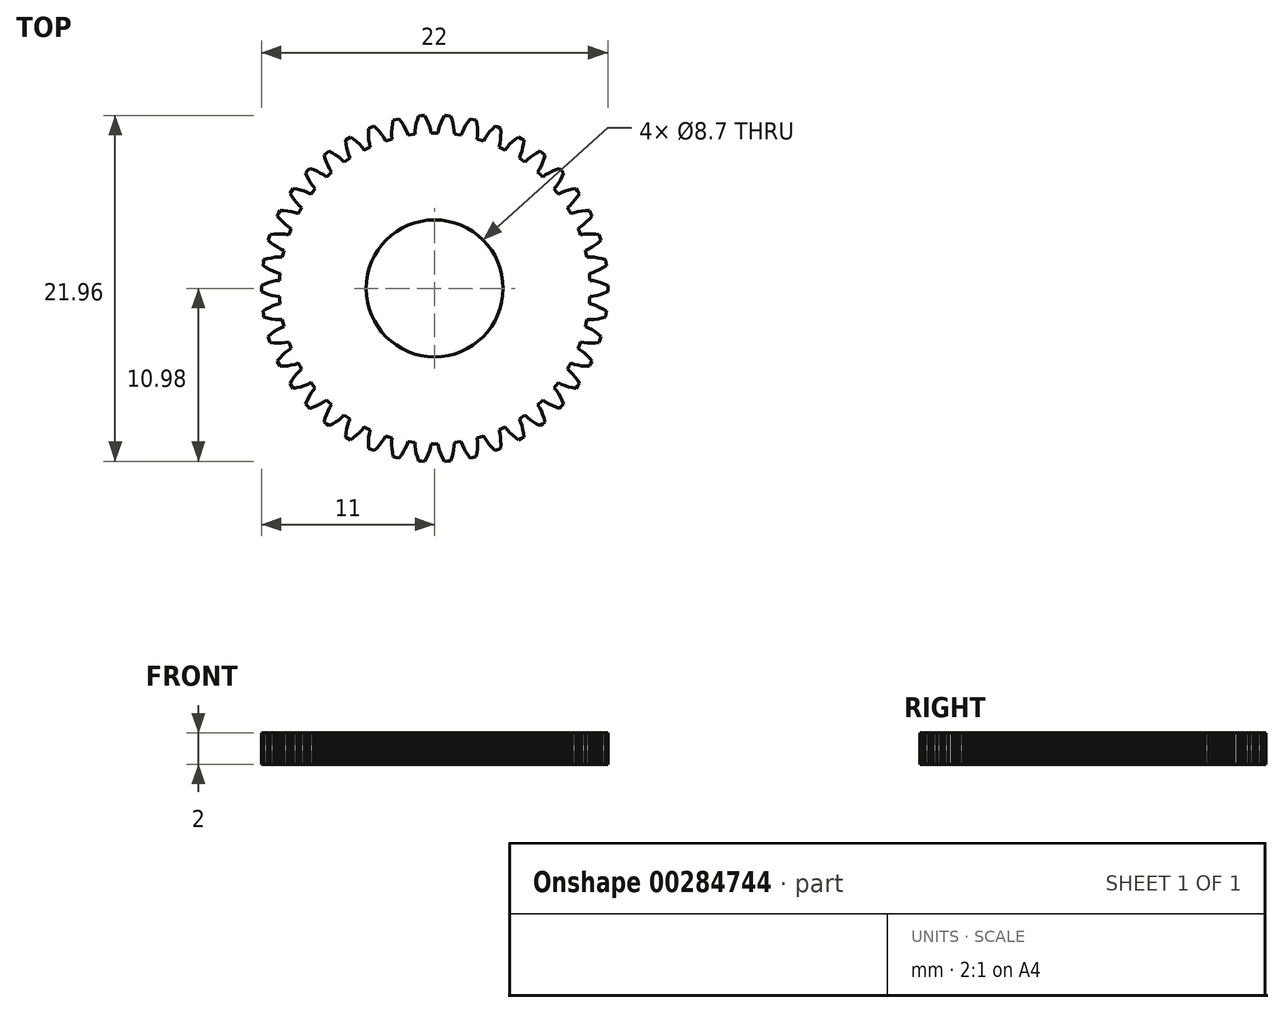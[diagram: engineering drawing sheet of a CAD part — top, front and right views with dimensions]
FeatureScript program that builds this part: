
annotation { "Feature Type Name" : "Feature", "Feature Type Description" : "" }
export const myFeature = defineFeature(function(context is Context, id is Id, definition is map)
    precondition{}
    {
        {
            var Q0;
            Q0=qCreatedBy(makeId("Top.planeOp"),FACE);
            var sketch = newSketch(context, id + "F0", { "sketchPlane" : qUnion([Q0])});
            skLineSegment(sketch, "E0", {"start": v(9.85, -0.74) * mm, "end": v(9.86, -0.52) * mm});
            skLineSegment(sketch, "E1", {"start": v(9.86, -0.52) * mm, "end": v(10.09, -0.5) * mm});
            skLineSegment(sketch, "E2", {"start": v(10.09, -0.5) * mm, "end": v(10.32, -0.44) * mm});
            skLineSegment(sketch, "E3", {"start": v(10.32, -0.44) * mm, "end": v(10.54, -0.38) * mm});
            skLineSegment(sketch, "E4", {"start": v(10.54, -0.38) * mm, "end": v(10.77, -0.3) * mm});
            skLineSegment(sketch, "E5", {"start": v(10.77, -0.3) * mm, "end": v(11, -0.2) * mm});
            skLineSegment(sketch, "E6", {"start": v(11, -0.2) * mm, "end": v(11, 0) * mm});
            skLineSegment(sketch, "E7", {"start": v(11, 0) * mm, "end": v(11, 0.2) * mm});
            skLineSegment(sketch, "E8", {"start": v(11, 0.2) * mm, "end": v(10.77, 0.3) * mm});
            skLineSegment(sketch, "E9", {"start": v(10.77, 0.3) * mm, "end": v(10.54, 0.38) * mm});
            skLineSegment(sketch, "E10", {"start": v(10.54, 0.38) * mm, "end": v(10.32, 0.44) * mm});
            skLineSegment(sketch, "E11", {"start": v(10.32, 0.44) * mm, "end": v(10.09, 0.5) * mm});
            skLineSegment(sketch, "E12", {"start": v(10.09, 0.5) * mm, "end": v(9.86, 0.52) * mm});
            skLineSegment(sketch, "E13", {"start": v(9.86, 0.52) * mm, "end": v(9.85, 0.74) * mm});
            skLineSegment(sketch, "E14", {"start": v(9.85, 0.74) * mm, "end": v(9.83, 0.96) * mm});
            skLineSegment(sketch, "E15", {"start": v(9.83, 0.96) * mm, "end": v(10.05, 1.02) * mm});
            skLineSegment(sketch, "E16", {"start": v(10.05, 1.02) * mm, "end": v(10.27, 1.1) * mm});
            skLineSegment(sketch, "E17", {"start": v(10.27, 1.1) * mm, "end": v(10.48, 1.2) * mm});
            skLineSegment(sketch, "E18", {"start": v(10.48, 1.2) * mm, "end": v(10.7, 1.32) * mm});
            skLineSegment(sketch, "E19", {"start": v(10.7, 1.32) * mm, "end": v(10.9, 1.45) * mm});
            skLineSegment(sketch, "E20", {"start": v(10.9, 1.45) * mm, "end": v(10.88, 1.64) * mm});
            skLineSegment(sketch, "E21", {"start": v(10.88, 1.64) * mm, "end": v(10.85, 1.83) * mm});
            skLineSegment(sketch, "E22", {"start": v(10.85, 1.83) * mm, "end": v(10.6, 1.9) * mm});
            skLineSegment(sketch, "E23", {"start": v(10.6, 1.9) * mm, "end": v(10.37, 1.94) * mm});
            skLineSegment(sketch, "E24", {"start": v(10.37, 1.94) * mm, "end": v(10.13, 1.98) * mm});
            skLineSegment(sketch, "E25", {"start": v(10.13, 1.98) * mm, "end": v(9.9, 2) * mm});
            skLineSegment(sketch, "E26", {"start": v(9.9, 2) * mm, "end": v(9.67, 1.98) * mm});
            skLineSegment(sketch, "E27", {"start": v(9.67, 1.98) * mm, "end": v(9.63, 2.2) * mm});
            skLineSegment(sketch, "E28", {"start": v(9.63, 2.2) * mm, "end": v(9.58, 2.41) * mm});
            skLineSegment(sketch, "E29", {"start": v(9.58, 2.41) * mm, "end": v(9.79, 2.5) * mm});
            skLineSegment(sketch, "E30", {"start": v(9.79, 2.5) * mm, "end": v(9.99, 2.62) * mm});
            skLineSegment(sketch, "E31", {"start": v(9.99, 2.62) * mm, "end": v(10.19, 2.75) * mm});
            skLineSegment(sketch, "E32", {"start": v(10.19, 2.75) * mm, "end": v(10.38, 2.9) * mm});
            skLineSegment(sketch, "E33", {"start": v(10.38, 2.9) * mm, "end": v(10.57, 3.06) * mm});
            skLineSegment(sketch, "E34", {"start": v(10.57, 3.06) * mm, "end": v(10.51, 3.24) * mm});
            skLineSegment(sketch, "E35", {"start": v(10.51, 3.24) * mm, "end": v(10.45, 3.42) * mm});
            skLineSegment(sketch, "E36", {"start": v(10.45, 3.42) * mm, "end": v(10.2, 3.45) * mm});
            skLineSegment(sketch, "E37", {"start": v(10.2, 3.45) * mm, "end": v(9.96, 3.47) * mm});
            skLineSegment(sketch, "E38", {"start": v(9.96, 3.47) * mm, "end": v(9.73, 3.47) * mm});
            skLineSegment(sketch, "E39", {"start": v(9.73, 3.47) * mm, "end": v(9.5, 3.45) * mm});
            skLineSegment(sketch, "E40", {"start": v(9.5, 3.45) * mm, "end": v(9.27, 3.4) * mm});
            skLineSegment(sketch, "E41", {"start": v(9.27, 3.4) * mm, "end": v(9.2, 3.6) * mm});
            skLineSegment(sketch, "E42", {"start": v(9.2, 3.6) * mm, "end": v(9.1, 3.81) * mm});
            skLineSegment(sketch, "E43", {"start": v(9.1, 3.81) * mm, "end": v(9.3, 3.93) * mm});
            skLineSegment(sketch, "E44", {"start": v(9.3, 3.93) * mm, "end": v(9.49, 4.08) * mm});
            skLineSegment(sketch, "E45", {"start": v(9.49, 4.08) * mm, "end": v(9.66, 4.24) * mm});
            skLineSegment(sketch, "E46", {"start": v(9.66, 4.24) * mm, "end": v(9.83, 4.41) * mm});
            skLineSegment(sketch, "E47", {"start": v(9.83, 4.41) * mm, "end": v(10, 4.6) * mm});
            skLineSegment(sketch, "E48", {"start": v(10, 4.6) * mm, "end": v(9.91, 4.77) * mm});
            skLineSegment(sketch, "E49", {"start": v(9.91, 4.77) * mm, "end": v(9.83, 4.94) * mm});
            skLineSegment(sketch, "E50", {"start": v(9.83, 4.94) * mm, "end": v(9.58, 4.94) * mm});
            skLineSegment(sketch, "E51", {"start": v(9.58, 4.94) * mm, "end": v(9.34, 4.91) * mm});
            skLineSegment(sketch, "E52", {"start": v(9.34, 4.91) * mm, "end": v(9.1, 4.88) * mm});
            skLineSegment(sketch, "E53", {"start": v(9.1, 4.88) * mm, "end": v(8.87, 4.82) * mm});
            skLineSegment(sketch, "E54", {"start": v(8.87, 4.82) * mm, "end": v(8.66, 4.74) * mm});
            skLineSegment(sketch, "E55", {"start": v(8.66, 4.74) * mm, "end": v(8.55, 4.94) * mm});
            skLineSegment(sketch, "E56", {"start": v(8.55, 4.94) * mm, "end": v(8.44, 5.13) * mm});
            skLineSegment(sketch, "E57", {"start": v(8.44, 5.13) * mm, "end": v(8.61, 5.27) * mm});
            skLineSegment(sketch, "E58", {"start": v(8.61, 5.27) * mm, "end": v(8.77, 5.44) * mm});
            skLineSegment(sketch, "E59", {"start": v(8.77, 5.44) * mm, "end": v(8.92, 5.63) * mm});
            skLineSegment(sketch, "E60", {"start": v(8.92, 5.63) * mm, "end": v(9.06, 5.83) * mm});
            skLineSegment(sketch, "E61", {"start": v(9.06, 5.83) * mm, "end": v(9.2, 6.04) * mm});
            skLineSegment(sketch, "E62", {"start": v(9.2, 6.04) * mm, "end": v(9.09, 6.2) * mm});
            skLineSegment(sketch, "E63", {"start": v(9.09, 6.2) * mm, "end": v(8.98, 6.35) * mm});
            skLineSegment(sketch, "E64", {"start": v(8.98, 6.35) * mm, "end": v(8.74, 6.3) * mm});
            skLineSegment(sketch, "E65", {"start": v(8.74, 6.3) * mm, "end": v(8.5, 6.25) * mm});
            skLineSegment(sketch, "E66", {"start": v(8.5, 6.25) * mm, "end": v(8.27, 6.18) * mm});
            skLineSegment(sketch, "E67", {"start": v(8.27, 6.18) * mm, "end": v(8.06, 6.1) * mm});
            skLineSegment(sketch, "E68", {"start": v(8.06, 6.1) * mm, "end": v(7.86, 5.98) * mm});
            skLineSegment(sketch, "E69", {"start": v(7.86, 5.98) * mm, "end": v(7.72, 6.16) * mm});
            skLineSegment(sketch, "E70", {"start": v(7.72, 6.16) * mm, "end": v(7.58, 6.33) * mm});
            skLineSegment(sketch, "E71", {"start": v(7.58, 6.33) * mm, "end": v(7.73, 6.5) * mm});
            skLineSegment(sketch, "E72", {"start": v(7.73, 6.5) * mm, "end": v(7.86, 6.7) * mm});
            skLineSegment(sketch, "E73", {"start": v(7.86, 6.7) * mm, "end": v(7.98, 6.9) * mm});
            skLineSegment(sketch, "E74", {"start": v(7.98, 6.9) * mm, "end": v(8.1, 7.11) * mm});
            skLineSegment(sketch, "E75", {"start": v(8.1, 7.11) * mm, "end": v(8.2, 7.34) * mm});
            skLineSegment(sketch, "E76", {"start": v(8.2, 7.34) * mm, "end": v(8.06, 7.48) * mm});
            skLineSegment(sketch, "E77", {"start": v(8.06, 7.48) * mm, "end": v(7.93, 7.62) * mm});
            skLineSegment(sketch, "E78", {"start": v(7.93, 7.62) * mm, "end": v(7.7, 7.54) * mm});
            skLineSegment(sketch, "E79", {"start": v(7.7, 7.54) * mm, "end": v(7.47, 7.45) * mm});
            skLineSegment(sketch, "E80", {"start": v(7.47, 7.45) * mm, "end": v(7.26, 7.34) * mm});
            skLineSegment(sketch, "E81", {"start": v(7.26, 7.34) * mm, "end": v(7.06, 7.22) * mm});
            skLineSegment(sketch, "E82", {"start": v(7.06, 7.22) * mm, "end": v(6.88, 7.09) * mm});
            skLineSegment(sketch, "E83", {"start": v(6.88, 7.09) * mm, "end": v(6.72, 7.24) * mm});
            skLineSegment(sketch, "E84", {"start": v(6.72, 7.24) * mm, "end": v(6.55, 7.39) * mm});
            skLineSegment(sketch, "E85", {"start": v(6.55, 7.39) * mm, "end": v(6.68, 7.58) * mm});
            skLineSegment(sketch, "E86", {"start": v(6.68, 7.58) * mm, "end": v(6.78, 7.79) * mm});
            skLineSegment(sketch, "E87", {"start": v(6.78, 7.79) * mm, "end": v(6.87, 8) * mm});
            skLineSegment(sketch, "E88", {"start": v(6.87, 8) * mm, "end": v(6.94, 8.24) * mm});
            skLineSegment(sketch, "E89", {"start": v(6.94, 8.24) * mm, "end": v(7, 8.48) * mm});
            skLineSegment(sketch, "E90", {"start": v(7, 8.48) * mm, "end": v(6.86, 8.6) * mm});
            skLineSegment(sketch, "E91", {"start": v(6.86, 8.6) * mm, "end": v(6.7, 8.72) * mm});
            skLineSegment(sketch, "E92", {"start": v(6.7, 8.72) * mm, "end": v(6.49, 8.6) * mm});
            skLineSegment(sketch, "E93", {"start": v(6.49, 8.6) * mm, "end": v(6.28, 8.48) * mm});
            skLineSegment(sketch, "E94", {"start": v(6.28, 8.48) * mm, "end": v(6.08, 8.34) * mm});
            skLineSegment(sketch, "E95", {"start": v(6.08, 8.34) * mm, "end": v(5.9, 8.2) * mm});
            skLineSegment(sketch, "E96", {"start": v(5.9, 8.2) * mm, "end": v(5.75, 8.03) * mm});
            skLineSegment(sketch, "E97", {"start": v(5.75, 8.03) * mm, "end": v(5.56, 8.16) * mm});
            skLineSegment(sketch, "E98", {"start": v(5.56, 8.16) * mm, "end": v(5.38, 8.28) * mm});
            skLineSegment(sketch, "E99", {"start": v(5.38, 8.28) * mm, "end": v(5.47, 8.49) * mm});
            skLineSegment(sketch, "E100", {"start": v(5.47, 8.49) * mm, "end": v(5.54, 8.71) * mm});
            skLineSegment(sketch, "E101", {"start": v(5.54, 8.71) * mm, "end": v(5.6, 8.94) * mm});
            skLineSegment(sketch, "E102", {"start": v(5.6, 8.94) * mm, "end": v(5.64, 9.18) * mm});
            skLineSegment(sketch, "E103", {"start": v(5.64, 9.18) * mm, "end": v(5.66, 9.43) * mm});
            skLineSegment(sketch, "E104", {"start": v(5.66, 9.43) * mm, "end": v(5.5, 9.53) * mm});
            skLineSegment(sketch, "E105", {"start": v(5.5, 9.53) * mm, "end": v(5.33, 9.62) * mm});
            skLineSegment(sketch, "E106", {"start": v(5.33, 9.62) * mm, "end": v(5.13, 9.47) * mm});
            skLineSegment(sketch, "E107", {"start": v(5.13, 9.47) * mm, "end": v(4.95, 9.32) * mm});
            skLineSegment(sketch, "E108", {"start": v(4.95, 9.32) * mm, "end": v(4.77, 9.16) * mm});
            skLineSegment(sketch, "E109", {"start": v(4.77, 9.16) * mm, "end": v(4.62, 8.98) * mm});
            skLineSegment(sketch, "E110", {"start": v(4.62, 8.98) * mm, "end": v(4.48, 8.8) * mm});
            skLineSegment(sketch, "E111", {"start": v(4.48, 8.8) * mm, "end": v(4.28, 8.9) * mm});
            skLineSegment(sketch, "E112", {"start": v(4.28, 8.9) * mm, "end": v(4.08, 9) * mm});
            skLineSegment(sketch, "E113", {"start": v(4.08, 9) * mm, "end": v(4.15, 9.21) * mm});
            skLineSegment(sketch, "E114", {"start": v(4.15, 9.21) * mm, "end": v(4.18, 9.44) * mm});
            skLineSegment(sketch, "E115", {"start": v(4.18, 9.44) * mm, "end": v(4.2, 9.68) * mm});
            skLineSegment(sketch, "E116", {"start": v(4.2, 9.68) * mm, "end": v(4.2, 9.92) * mm});
            skLineSegment(sketch, "E117", {"start": v(4.2, 9.92) * mm, "end": v(4.2, 10.17) * mm});
            skLineSegment(sketch, "E118", {"start": v(4.2, 10.17) * mm, "end": v(4.02, 10.24) * mm});
            skLineSegment(sketch, "E119", {"start": v(4.02, 10.24) * mm, "end": v(3.84, 10.3) * mm});
            skLineSegment(sketch, "E120", {"start": v(3.84, 10.3) * mm, "end": v(3.66, 10.13) * mm});
            skLineSegment(sketch, "E121", {"start": v(3.66, 10.13) * mm, "end": v(3.5, 9.95) * mm});
            skLineSegment(sketch, "E122", {"start": v(3.5, 9.95) * mm, "end": v(3.35, 9.76) * mm});
            skLineSegment(sketch, "E123", {"start": v(3.35, 9.76) * mm, "end": v(3.23, 9.57) * mm});
            skLineSegment(sketch, "E124", {"start": v(3.23, 9.57) * mm, "end": v(3.12, 9.37) * mm});
            skLineSegment(sketch, "E125", {"start": v(3.12, 9.37) * mm, "end": v(2.91, 9.44) * mm});
            skLineSegment(sketch, "E126", {"start": v(2.91, 9.44) * mm, "end": v(2.7, 9.5) * mm});
            skLineSegment(sketch, "E127", {"start": v(2.7, 9.5) * mm, "end": v(2.73, 9.73) * mm});
            skLineSegment(sketch, "E128", {"start": v(2.73, 9.73) * mm, "end": v(2.73, 9.96) * mm});
            skLineSegment(sketch, "E129", {"start": v(2.73, 9.96) * mm, "end": v(2.71, 10.2) * mm});
            skLineSegment(sketch, "E130", {"start": v(2.71, 10.2) * mm, "end": v(2.68, 10.44) * mm});
            skLineSegment(sketch, "E131", {"start": v(2.68, 10.44) * mm, "end": v(2.63, 10.68) * mm});
            skLineSegment(sketch, "E132", {"start": v(2.63, 10.68) * mm, "end": v(2.45, 10.72) * mm});
            skLineSegment(sketch, "E133", {"start": v(2.45, 10.72) * mm, "end": v(2.26, 10.77) * mm});
            skLineSegment(sketch, "E134", {"start": v(2.26, 10.77) * mm, "end": v(2.11, 10.57) * mm});
            skLineSegment(sketch, "E135", {"start": v(2.11, 10.57) * mm, "end": v(1.98, 10.36) * mm});
            skLineSegment(sketch, "E136", {"start": v(1.98, 10.36) * mm, "end": v(1.86, 10.16) * mm});
            skLineSegment(sketch, "E137", {"start": v(1.86, 10.16) * mm, "end": v(1.76, 9.94) * mm});
            skLineSegment(sketch, "E138", {"start": v(1.76, 9.94) * mm, "end": v(1.7, 9.73) * mm});
            skLineSegment(sketch, "E139", {"start": v(1.7, 9.73) * mm, "end": v(1.47, 9.76) * mm});
            skLineSegment(sketch, "E140", {"start": v(1.47, 9.76) * mm, "end": v(1.25, 9.8) * mm});
            skLineSegment(sketch, "E141", {"start": v(1.25, 9.8) * mm, "end": v(1.25, 10.02) * mm});
            skLineSegment(sketch, "E142", {"start": v(1.25, 10.02) * mm, "end": v(1.21, 10.25) * mm});
            skLineSegment(sketch, "E143", {"start": v(1.21, 10.25) * mm, "end": v(1.16, 10.49) * mm});
            skLineSegment(sketch, "E144", {"start": v(1.16, 10.49) * mm, "end": v(1.1, 10.72) * mm});
            skLineSegment(sketch, "E145", {"start": v(1.1, 10.72) * mm, "end": v(1.01, 10.95) * mm});
            skLineSegment(sketch, "E146", {"start": v(1.01, 10.95) * mm, "end": v(0.82, 10.97) * mm});
            skLineSegment(sketch, "E147", {"start": v(0.82, 10.97) * mm, "end": v(0.63, 10.98) * mm});
            skLineSegment(sketch, "E148", {"start": v(0.63, 10.98) * mm, "end": v(0.51, 10.76) * mm});
            skLineSegment(sketch, "E149", {"start": v(0.51, 10.76) * mm, "end": v(0.41, 10.54) * mm});
            skLineSegment(sketch, "E150", {"start": v(0.41, 10.54) * mm, "end": v(0.33, 10.32) * mm});
            skLineSegment(sketch, "E151", {"start": v(0.33, 10.32) * mm, "end": v(0.26, 10.1) * mm});
            skLineSegment(sketch, "E152", {"start": v(0.26, 10.1) * mm, "end": v(0.22, 9.87) * mm});
            skLineSegment(sketch, "E153", {"start": v(0.22, 9.87) * mm, "end": v(0, 9.88) * mm});
            skLineSegment(sketch, "E154", {"start": v(0, 9.88) * mm, "end": v(-0.22, 9.87) * mm});
            skLineSegment(sketch, "E155", {"start": v(-0.22, 9.87) * mm, "end": v(-0.26, 10.1) * mm});
            skLineSegment(sketch, "E156", {"start": v(-0.26, 10.1) * mm, "end": v(-0.33, 10.32) * mm});
            skLineSegment(sketch, "E157", {"start": v(-0.33, 10.32) * mm, "end": v(-0.41, 10.54) * mm});
            skLineSegment(sketch, "E158", {"start": v(-0.41, 10.54) * mm, "end": v(-0.51, 10.76) * mm});
            skLineSegment(sketch, "E159", {"start": v(-0.51, 10.76) * mm, "end": v(-0.63, 10.98) * mm});
            skLineSegment(sketch, "E160", {"start": v(-0.63, 10.98) * mm, "end": v(-0.82, 10.97) * mm});
            skLineSegment(sketch, "E161", {"start": v(-0.82, 10.97) * mm, "end": v(-1.01, 10.95) * mm});
            skLineSegment(sketch, "E162", {"start": v(-1.01, 10.95) * mm, "end": v(-1.1, 10.72) * mm});
            skLineSegment(sketch, "E163", {"start": v(-1.1, 10.72) * mm, "end": v(-1.16, 10.49) * mm});
            skLineSegment(sketch, "E164", {"start": v(-1.16, 10.49) * mm, "end": v(-1.21, 10.25) * mm});
            skLineSegment(sketch, "E165", {"start": v(-1.21, 10.25) * mm, "end": v(-1.25, 10.02) * mm});
            skLineSegment(sketch, "E166", {"start": v(-1.25, 10.02) * mm, "end": v(-1.25, 9.8) * mm});
            skLineSegment(sketch, "E167", {"start": v(-1.25, 9.8) * mm, "end": v(-1.47, 9.76) * mm});
            skLineSegment(sketch, "E168", {"start": v(-1.47, 9.76) * mm, "end": v(-1.7, 9.73) * mm});
            skLineSegment(sketch, "E169", {"start": v(-1.7, 9.73) * mm, "end": v(-1.76, 9.94) * mm});
            skLineSegment(sketch, "E170", {"start": v(-1.76, 9.94) * mm, "end": v(-1.86, 10.16) * mm});
            skLineSegment(sketch, "E171", {"start": v(-1.86, 10.16) * mm, "end": v(-1.98, 10.36) * mm});
            skLineSegment(sketch, "E172", {"start": v(-1.98, 10.36) * mm, "end": v(-2.11, 10.57) * mm});
            skLineSegment(sketch, "E173", {"start": v(-2.11, 10.57) * mm, "end": v(-2.26, 10.77) * mm});
            skLineSegment(sketch, "E174", {"start": v(-2.26, 10.77) * mm, "end": v(-2.45, 10.72) * mm});
            skLineSegment(sketch, "E175", {"start": v(-2.45, 10.72) * mm, "end": v(-2.63, 10.68) * mm});
            skLineSegment(sketch, "E176", {"start": v(-2.63, 10.68) * mm, "end": v(-2.68, 10.44) * mm});
            skLineSegment(sketch, "E177", {"start": v(-2.68, 10.44) * mm, "end": v(-2.71, 10.2) * mm});
            skLineSegment(sketch, "E178", {"start": v(-2.71, 10.2) * mm, "end": v(-2.73, 9.96) * mm});
            skLineSegment(sketch, "E179", {"start": v(-2.73, 9.96) * mm, "end": v(-2.73, 9.73) * mm});
            skLineSegment(sketch, "E180", {"start": v(-2.73, 9.73) * mm, "end": v(-2.7, 9.5) * mm});
            skLineSegment(sketch, "E181", {"start": v(-2.7, 9.5) * mm, "end": v(-2.91, 9.44) * mm});
            skLineSegment(sketch, "E182", {"start": v(-2.91, 9.44) * mm, "end": v(-3.12, 9.37) * mm});
            skLineSegment(sketch, "E183", {"start": v(-3.12, 9.37) * mm, "end": v(-3.23, 9.57) * mm});
            skLineSegment(sketch, "E184", {"start": v(-3.23, 9.57) * mm, "end": v(-3.35, 9.76) * mm});
            skLineSegment(sketch, "E185", {"start": v(-3.35, 9.76) * mm, "end": v(-3.5, 9.95) * mm});
            skLineSegment(sketch, "E186", {"start": v(-3.5, 9.95) * mm, "end": v(-3.66, 10.13) * mm});
            skLineSegment(sketch, "E187", {"start": v(-3.66, 10.13) * mm, "end": v(-3.84, 10.3) * mm});
            skLineSegment(sketch, "E188", {"start": v(-3.84, 10.3) * mm, "end": v(-4.02, 10.24) * mm});
            skLineSegment(sketch, "E189", {"start": v(-4.02, 10.24) * mm, "end": v(-4.2, 10.17) * mm});
            skLineSegment(sketch, "E190", {"start": v(-4.2, 10.17) * mm, "end": v(-4.2, 9.92) * mm});
            skLineSegment(sketch, "E191", {"start": v(-4.2, 9.92) * mm, "end": v(-4.2, 9.68) * mm});
            skLineSegment(sketch, "E192", {"start": v(-4.2, 9.68) * mm, "end": v(-4.18, 9.44) * mm});
            skLineSegment(sketch, "E193", {"start": v(-4.18, 9.44) * mm, "end": v(-4.15, 9.21) * mm});
            skLineSegment(sketch, "E194", {"start": v(-4.15, 9.21) * mm, "end": v(-4.08, 9) * mm});
            skLineSegment(sketch, "E195", {"start": v(-4.08, 9) * mm, "end": v(-4.28, 8.9) * mm});
            skLineSegment(sketch, "E196", {"start": v(-4.28, 8.9) * mm, "end": v(-4.48, 8.8) * mm});
            skLineSegment(sketch, "E197", {"start": v(-4.48, 8.8) * mm, "end": v(-4.62, 8.98) * mm});
            skLineSegment(sketch, "E198", {"start": v(-4.62, 8.98) * mm, "end": v(-4.77, 9.16) * mm});
            skLineSegment(sketch, "E199", {"start": v(-4.77, 9.16) * mm, "end": v(-4.95, 9.32) * mm});
            skLineSegment(sketch, "E200", {"start": v(-4.95, 9.32) * mm, "end": v(-5.13, 9.47) * mm});
            skLineSegment(sketch, "E201", {"start": v(-5.13, 9.47) * mm, "end": v(-5.33, 9.62) * mm});
            skLineSegment(sketch, "E202", {"start": v(-5.33, 9.62) * mm, "end": v(-5.5, 9.53) * mm});
            skLineSegment(sketch, "E203", {"start": v(-5.5, 9.53) * mm, "end": v(-5.66, 9.43) * mm});
            skLineSegment(sketch, "E204", {"start": v(-5.66, 9.43) * mm, "end": v(-5.64, 9.18) * mm});
            skLineSegment(sketch, "E205", {"start": v(-5.64, 9.18) * mm, "end": v(-5.6, 8.94) * mm});
            skLineSegment(sketch, "E206", {"start": v(-5.6, 8.94) * mm, "end": v(-5.54, 8.71) * mm});
            skLineSegment(sketch, "E207", {"start": v(-5.54, 8.71) * mm, "end": v(-5.47, 8.49) * mm});
            skLineSegment(sketch, "E208", {"start": v(-5.47, 8.49) * mm, "end": v(-5.38, 8.28) * mm});
            skLineSegment(sketch, "E209", {"start": v(-5.38, 8.28) * mm, "end": v(-5.56, 8.16) * mm});
            skLineSegment(sketch, "E210", {"start": v(-5.56, 8.16) * mm, "end": v(-5.75, 8.03) * mm});
            skLineSegment(sketch, "E211", {"start": v(-5.75, 8.03) * mm, "end": v(-5.9, 8.2) * mm});
            skLineSegment(sketch, "E212", {"start": v(-5.9, 8.2) * mm, "end": v(-6.08, 8.34) * mm});
            skLineSegment(sketch, "E213", {"start": v(-6.08, 8.34) * mm, "end": v(-6.28, 8.48) * mm});
            skLineSegment(sketch, "E214", {"start": v(-6.28, 8.48) * mm, "end": v(-6.49, 8.6) * mm});
            skLineSegment(sketch, "E215", {"start": v(-6.49, 8.6) * mm, "end": v(-6.7, 8.72) * mm});
            skLineSegment(sketch, "E216", {"start": v(-6.7, 8.72) * mm, "end": v(-6.86, 8.6) * mm});
            skLineSegment(sketch, "E217", {"start": v(-6.86, 8.6) * mm, "end": v(-7, 8.48) * mm});
            skLineSegment(sketch, "E218", {"start": v(-7, 8.48) * mm, "end": v(-6.94, 8.24) * mm});
            skLineSegment(sketch, "E219", {"start": v(-6.94, 8.24) * mm, "end": v(-6.87, 8) * mm});
            skLineSegment(sketch, "E220", {"start": v(-6.87, 8) * mm, "end": v(-6.78, 7.79) * mm});
            skLineSegment(sketch, "E221", {"start": v(-6.78, 7.79) * mm, "end": v(-6.68, 7.58) * mm});
            skLineSegment(sketch, "E222", {"start": v(-6.68, 7.58) * mm, "end": v(-6.55, 7.39) * mm});
            skLineSegment(sketch, "E223", {"start": v(-6.55, 7.39) * mm, "end": v(-6.72, 7.24) * mm});
            skLineSegment(sketch, "E224", {"start": v(-6.72, 7.24) * mm, "end": v(-6.88, 7.09) * mm});
            skLineSegment(sketch, "E225", {"start": v(-6.88, 7.09) * mm, "end": v(-7.06, 7.22) * mm});
            skLineSegment(sketch, "E226", {"start": v(-7.06, 7.22) * mm, "end": v(-7.26, 7.34) * mm});
            skLineSegment(sketch, "E227", {"start": v(-7.26, 7.34) * mm, "end": v(-7.47, 7.45) * mm});
            skLineSegment(sketch, "E228", {"start": v(-7.47, 7.45) * mm, "end": v(-7.7, 7.54) * mm});
            skLineSegment(sketch, "E229", {"start": v(-7.7, 7.54) * mm, "end": v(-7.93, 7.62) * mm});
            skLineSegment(sketch, "E230", {"start": v(-7.93, 7.62) * mm, "end": v(-8.06, 7.48) * mm});
            skLineSegment(sketch, "E231", {"start": v(-8.06, 7.48) * mm, "end": v(-8.2, 7.34) * mm});
            skLineSegment(sketch, "E232", {"start": v(-8.2, 7.34) * mm, "end": v(-8.1, 7.11) * mm});
            skLineSegment(sketch, "E233", {"start": v(-8.1, 7.11) * mm, "end": v(-7.98, 6.9) * mm});
            skLineSegment(sketch, "E234", {"start": v(-7.98, 6.9) * mm, "end": v(-7.86, 6.7) * mm});
            skLineSegment(sketch, "E235", {"start": v(-7.86, 6.7) * mm, "end": v(-7.73, 6.5) * mm});
            skLineSegment(sketch, "E236", {"start": v(-7.73, 6.5) * mm, "end": v(-7.58, 6.33) * mm});
            skLineSegment(sketch, "E237", {"start": v(-7.58, 6.33) * mm, "end": v(-7.72, 6.16) * mm});
            skLineSegment(sketch, "E238", {"start": v(-7.72, 6.16) * mm, "end": v(-7.86, 5.98) * mm});
            skLineSegment(sketch, "E239", {"start": v(-7.86, 5.98) * mm, "end": v(-8.06, 6.1) * mm});
            skLineSegment(sketch, "E240", {"start": v(-8.06, 6.1) * mm, "end": v(-8.27, 6.18) * mm});
            skLineSegment(sketch, "E241", {"start": v(-8.27, 6.18) * mm, "end": v(-8.5, 6.25) * mm});
            skLineSegment(sketch, "E242", {"start": v(-8.5, 6.25) * mm, "end": v(-8.74, 6.3) * mm});
            skLineSegment(sketch, "E243", {"start": v(-8.74, 6.3) * mm, "end": v(-8.98, 6.35) * mm});
            skLineSegment(sketch, "E244", {"start": v(-8.98, 6.35) * mm, "end": v(-9.09, 6.2) * mm});
            skLineSegment(sketch, "E245", {"start": v(-9.09, 6.2) * mm, "end": v(-9.2, 6.04) * mm});
            skLineSegment(sketch, "E246", {"start": v(-9.2, 6.04) * mm, "end": v(-9.06, 5.83) * mm});
            skLineSegment(sketch, "E247", {"start": v(-9.06, 5.83) * mm, "end": v(-8.92, 5.63) * mm});
            skLineSegment(sketch, "E248", {"start": v(-8.92, 5.63) * mm, "end": v(-8.77, 5.44) * mm});
            skLineSegment(sketch, "E249", {"start": v(-8.77, 5.44) * mm, "end": v(-8.61, 5.27) * mm});
            skLineSegment(sketch, "E250", {"start": v(-8.61, 5.27) * mm, "end": v(-8.44, 5.13) * mm});
            skLineSegment(sketch, "E251", {"start": v(-8.44, 5.13) * mm, "end": v(-8.55, 4.94) * mm});
            skLineSegment(sketch, "E252", {"start": v(-8.55, 4.94) * mm, "end": v(-8.66, 4.74) * mm});
            skLineSegment(sketch, "E253", {"start": v(-8.66, 4.74) * mm, "end": v(-8.87, 4.82) * mm});
            skLineSegment(sketch, "E254", {"start": v(-8.87, 4.82) * mm, "end": v(-9.1, 4.88) * mm});
            skLineSegment(sketch, "E255", {"start": v(-9.1, 4.88) * mm, "end": v(-9.34, 4.91) * mm});
            skLineSegment(sketch, "E256", {"start": v(-9.34, 4.91) * mm, "end": v(-9.58, 4.94) * mm});
            skLineSegment(sketch, "E257", {"start": v(-9.58, 4.94) * mm, "end": v(-9.83, 4.94) * mm});
            skLineSegment(sketch, "E258", {"start": v(-9.83, 4.94) * mm, "end": v(-9.91, 4.77) * mm});
            skLineSegment(sketch, "E259", {"start": v(-9.91, 4.77) * mm, "end": v(-10, 4.6) * mm});
            skLineSegment(sketch, "E260", {"start": v(-10, 4.6) * mm, "end": v(-9.83, 4.41) * mm});
            skLineSegment(sketch, "E261", {"start": v(-9.83, 4.41) * mm, "end": v(-9.66, 4.24) * mm});
            skLineSegment(sketch, "E262", {"start": v(-9.66, 4.24) * mm, "end": v(-9.49, 4.08) * mm});
            skLineSegment(sketch, "E263", {"start": v(-9.49, 4.08) * mm, "end": v(-9.3, 3.93) * mm});
            skLineSegment(sketch, "E264", {"start": v(-9.3, 3.93) * mm, "end": v(-9.1, 3.81) * mm});
            skLineSegment(sketch, "E265", {"start": v(-9.1, 3.81) * mm, "end": v(-9.2, 3.6) * mm});
            skLineSegment(sketch, "E266", {"start": v(-9.2, 3.6) * mm, "end": v(-9.27, 3.4) * mm});
            skLineSegment(sketch, "E267", {"start": v(-9.27, 3.4) * mm, "end": v(-9.5, 3.45) * mm});
            skLineSegment(sketch, "E268", {"start": v(-9.5, 3.45) * mm, "end": v(-9.73, 3.47) * mm});
            skLineSegment(sketch, "E269", {"start": v(-9.73, 3.47) * mm, "end": v(-9.96, 3.47) * mm});
            skLineSegment(sketch, "E270", {"start": v(-9.96, 3.47) * mm, "end": v(-10.2, 3.45) * mm});
            skLineSegment(sketch, "E271", {"start": v(-10.2, 3.45) * mm, "end": v(-10.45, 3.42) * mm});
            skLineSegment(sketch, "E272", {"start": v(-10.45, 3.42) * mm, "end": v(-10.51, 3.24) * mm});
            skLineSegment(sketch, "E273", {"start": v(-10.51, 3.24) * mm, "end": v(-10.57, 3.06) * mm});
            skLineSegment(sketch, "E274", {"start": v(-10.57, 3.06) * mm, "end": v(-10.38, 2.9) * mm});
            skLineSegment(sketch, "E275", {"start": v(-10.38, 2.9) * mm, "end": v(-10.19, 2.75) * mm});
            skLineSegment(sketch, "E276", {"start": v(-10.19, 2.75) * mm, "end": v(-9.99, 2.62) * mm});
            skLineSegment(sketch, "E277", {"start": v(-9.99, 2.62) * mm, "end": v(-9.79, 2.5) * mm});
            skLineSegment(sketch, "E278", {"start": v(-9.79, 2.5) * mm, "end": v(-9.58, 2.41) * mm});
            skLineSegment(sketch, "E279", {"start": v(-9.58, 2.41) * mm, "end": v(-9.63, 2.2) * mm});
            skLineSegment(sketch, "E280", {"start": v(-9.63, 2.2) * mm, "end": v(-9.67, 1.98) * mm});
            skLineSegment(sketch, "E281", {"start": v(-9.67, 1.98) * mm, "end": v(-9.9, 2) * mm});
            skLineSegment(sketch, "E282", {"start": v(-9.9, 2) * mm, "end": v(-10.13, 1.98) * mm});
            skLineSegment(sketch, "E283", {"start": v(-10.13, 1.98) * mm, "end": v(-10.37, 1.94) * mm});
            skLineSegment(sketch, "E284", {"start": v(-10.37, 1.94) * mm, "end": v(-10.6, 1.9) * mm});
            skLineSegment(sketch, "E285", {"start": v(-10.6, 1.9) * mm, "end": v(-10.85, 1.83) * mm});
            skLineSegment(sketch, "E286", {"start": v(-10.85, 1.83) * mm, "end": v(-10.88, 1.64) * mm});
            skLineSegment(sketch, "E287", {"start": v(-10.88, 1.64) * mm, "end": v(-10.9, 1.45) * mm});
            skLineSegment(sketch, "E288", {"start": v(-10.9, 1.45) * mm, "end": v(-10.7, 1.32) * mm});
            skLineSegment(sketch, "E289", {"start": v(-10.7, 1.32) * mm, "end": v(-10.48, 1.2) * mm});
            skLineSegment(sketch, "E290", {"start": v(-10.48, 1.2) * mm, "end": v(-10.27, 1.1) * mm});
            skLineSegment(sketch, "E291", {"start": v(-10.27, 1.1) * mm, "end": v(-10.05, 1.02) * mm});
            skLineSegment(sketch, "E292", {"start": v(-10.05, 1.02) * mm, "end": v(-9.83, 0.96) * mm});
            skLineSegment(sketch, "E293", {"start": v(-9.83, 0.96) * mm, "end": v(-9.85, 0.74) * mm});
            skLineSegment(sketch, "E294", {"start": v(-9.85, 0.74) * mm, "end": v(-9.86, 0.52) * mm});
            skLineSegment(sketch, "E295", {"start": v(-9.86, 0.52) * mm, "end": v(-10.09, 0.5) * mm});
            skLineSegment(sketch, "E296", {"start": v(-10.09, 0.5) * mm, "end": v(-10.32, 0.44) * mm});
            skLineSegment(sketch, "E297", {"start": v(-10.32, 0.44) * mm, "end": v(-10.54, 0.38) * mm});
            skLineSegment(sketch, "E298", {"start": v(-10.54, 0.38) * mm, "end": v(-10.77, 0.3) * mm});
            skLineSegment(sketch, "E299", {"start": v(-10.77, 0.3) * mm, "end": v(-11, 0.2) * mm});
            skLineSegment(sketch, "E300", {"start": v(-11, 0.2) * mm, "end": v(-11, 0) * mm});
            skLineSegment(sketch, "E301", {"start": v(-11, 0) * mm, "end": v(-11, -0.2) * mm});
            skLineSegment(sketch, "E302", {"start": v(-11, -0.2) * mm, "end": v(-10.77, -0.3) * mm});
            skLineSegment(sketch, "E303", {"start": v(-10.77, -0.3) * mm, "end": v(-10.54, -0.38) * mm});
            skLineSegment(sketch, "E304", {"start": v(-10.54, -0.38) * mm, "end": v(-10.32, -0.44) * mm});
            skLineSegment(sketch, "E305", {"start": v(-10.32, -0.44) * mm, "end": v(-10.09, -0.5) * mm});
            skLineSegment(sketch, "E306", {"start": v(-10.09, -0.5) * mm, "end": v(-9.86, -0.52) * mm});
            skLineSegment(sketch, "E307", {"start": v(-9.86, -0.52) * mm, "end": v(-9.85, -0.74) * mm});
            skLineSegment(sketch, "E308", {"start": v(-9.85, -0.74) * mm, "end": v(-9.83, -0.96) * mm});
            skLineSegment(sketch, "E309", {"start": v(-9.83, -0.96) * mm, "end": v(-10.05, -1.02) * mm});
            skLineSegment(sketch, "E310", {"start": v(-10.05, -1.02) * mm, "end": v(-10.27, -1.1) * mm});
            skLineSegment(sketch, "E311", {"start": v(-10.27, -1.1) * mm, "end": v(-10.48, -1.2) * mm});
            skLineSegment(sketch, "E312", {"start": v(-10.48, -1.2) * mm, "end": v(-10.7, -1.32) * mm});
            skLineSegment(sketch, "E313", {"start": v(-10.7, -1.32) * mm, "end": v(-10.9, -1.45) * mm});
            skLineSegment(sketch, "E314", {"start": v(-10.9, -1.45) * mm, "end": v(-10.88, -1.64) * mm});
            skLineSegment(sketch, "E315", {"start": v(-10.88, -1.64) * mm, "end": v(-10.85, -1.83) * mm});
            skLineSegment(sketch, "E316", {"start": v(-10.85, -1.83) * mm, "end": v(-10.6, -1.9) * mm});
            skLineSegment(sketch, "E317", {"start": v(-10.6, -1.9) * mm, "end": v(-10.37, -1.94) * mm});
            skLineSegment(sketch, "E318", {"start": v(-10.37, -1.94) * mm, "end": v(-10.13, -1.98) * mm});
            skLineSegment(sketch, "E319", {"start": v(-10.13, -1.98) * mm, "end": v(-9.9, -2) * mm});
            skLineSegment(sketch, "E320", {"start": v(-9.9, -2) * mm, "end": v(-9.67, -1.98) * mm});
            skLineSegment(sketch, "E321", {"start": v(-9.67, -1.98) * mm, "end": v(-9.63, -2.2) * mm});
            skLineSegment(sketch, "E322", {"start": v(-9.63, -2.2) * mm, "end": v(-9.58, -2.41) * mm});
            skLineSegment(sketch, "E323", {"start": v(-9.58, -2.41) * mm, "end": v(-9.79, -2.5) * mm});
            skLineSegment(sketch, "E324", {"start": v(-9.79, -2.5) * mm, "end": v(-9.99, -2.62) * mm});
            skLineSegment(sketch, "E325", {"start": v(-9.99, -2.62) * mm, "end": v(-10.19, -2.75) * mm});
            skLineSegment(sketch, "E326", {"start": v(-10.19, -2.75) * mm, "end": v(-10.38, -2.9) * mm});
            skLineSegment(sketch, "E327", {"start": v(-10.38, -2.9) * mm, "end": v(-10.57, -3.06) * mm});
            skLineSegment(sketch, "E328", {"start": v(-10.57, -3.06) * mm, "end": v(-10.51, -3.24) * mm});
            skLineSegment(sketch, "E329", {"start": v(-10.51, -3.24) * mm, "end": v(-10.45, -3.42) * mm});
            skLineSegment(sketch, "E330", {"start": v(-10.45, -3.42) * mm, "end": v(-10.2, -3.45) * mm});
            skLineSegment(sketch, "E331", {"start": v(-10.2, -3.45) * mm, "end": v(-9.96, -3.47) * mm});
            skLineSegment(sketch, "E332", {"start": v(-9.96, -3.47) * mm, "end": v(-9.73, -3.47) * mm});
            skLineSegment(sketch, "E333", {"start": v(-9.73, -3.47) * mm, "end": v(-9.5, -3.45) * mm});
            skLineSegment(sketch, "E334", {"start": v(-9.5, -3.45) * mm, "end": v(-9.27, -3.4) * mm});
            skLineSegment(sketch, "E335", {"start": v(-9.27, -3.4) * mm, "end": v(-9.2, -3.6) * mm});
            skLineSegment(sketch, "E336", {"start": v(-9.2, -3.6) * mm, "end": v(-9.1, -3.81) * mm});
            skLineSegment(sketch, "E337", {"start": v(-9.1, -3.81) * mm, "end": v(-9.3, -3.93) * mm});
            skLineSegment(sketch, "E338", {"start": v(-9.3, -3.93) * mm, "end": v(-9.49, -4.08) * mm});
            skLineSegment(sketch, "E339", {"start": v(-9.49, -4.08) * mm, "end": v(-9.66, -4.24) * mm});
            skLineSegment(sketch, "E340", {"start": v(-9.66, -4.24) * mm, "end": v(-9.83, -4.41) * mm});
            skLineSegment(sketch, "E341", {"start": v(-9.83, -4.41) * mm, "end": v(-10, -4.6) * mm});
            skLineSegment(sketch, "E342", {"start": v(-10, -4.6) * mm, "end": v(-9.91, -4.77) * mm});
            skLineSegment(sketch, "E343", {"start": v(-9.91, -4.77) * mm, "end": v(-9.83, -4.94) * mm});
            skLineSegment(sketch, "E344", {"start": v(-9.83, -4.94) * mm, "end": v(-9.58, -4.94) * mm});
            skLineSegment(sketch, "E345", {"start": v(-9.58, -4.94) * mm, "end": v(-9.34, -4.91) * mm});
            skLineSegment(sketch, "E346", {"start": v(-9.34, -4.91) * mm, "end": v(-9.1, -4.88) * mm});
            skLineSegment(sketch, "E347", {"start": v(-9.1, -4.88) * mm, "end": v(-8.87, -4.82) * mm});
            skLineSegment(sketch, "E348", {"start": v(-8.87, -4.82) * mm, "end": v(-8.66, -4.74) * mm});
            skLineSegment(sketch, "E349", {"start": v(-8.66, -4.74) * mm, "end": v(-8.55, -4.94) * mm});
            skLineSegment(sketch, "E350", {"start": v(-8.55, -4.94) * mm, "end": v(-8.44, -5.13) * mm});
            skLineSegment(sketch, "E351", {"start": v(-8.44, -5.13) * mm, "end": v(-8.61, -5.27) * mm});
            skLineSegment(sketch, "E352", {"start": v(-8.61, -5.27) * mm, "end": v(-8.77, -5.44) * mm});
            skLineSegment(sketch, "E353", {"start": v(-8.77, -5.44) * mm, "end": v(-8.92, -5.63) * mm});
            skLineSegment(sketch, "E354", {"start": v(-8.92, -5.63) * mm, "end": v(-9.06, -5.83) * mm});
            skLineSegment(sketch, "E355", {"start": v(-9.06, -5.83) * mm, "end": v(-9.2, -6.04) * mm});
            skLineSegment(sketch, "E356", {"start": v(-9.2, -6.04) * mm, "end": v(-9.09, -6.2) * mm});
            skLineSegment(sketch, "E357", {"start": v(-9.09, -6.2) * mm, "end": v(-8.98, -6.35) * mm});
            skLineSegment(sketch, "E358", {"start": v(-8.98, -6.35) * mm, "end": v(-8.74, -6.3) * mm});
            skLineSegment(sketch, "E359", {"start": v(-8.74, -6.3) * mm, "end": v(-8.5, -6.25) * mm});
            skLineSegment(sketch, "E360", {"start": v(-8.5, -6.25) * mm, "end": v(-8.27, -6.18) * mm});
            skLineSegment(sketch, "E361", {"start": v(-8.27, -6.18) * mm, "end": v(-8.06, -6.1) * mm});
            skLineSegment(sketch, "E362", {"start": v(-8.06, -6.1) * mm, "end": v(-7.86, -5.98) * mm});
            skLineSegment(sketch, "E363", {"start": v(-7.86, -5.98) * mm, "end": v(-7.72, -6.16) * mm});
            skLineSegment(sketch, "E364", {"start": v(-7.72, -6.16) * mm, "end": v(-7.58, -6.33) * mm});
            skLineSegment(sketch, "E365", {"start": v(-7.58, -6.33) * mm, "end": v(-7.73, -6.5) * mm});
            skLineSegment(sketch, "E366", {"start": v(-7.73, -6.5) * mm, "end": v(-7.86, -6.7) * mm});
            skLineSegment(sketch, "E367", {"start": v(-7.86, -6.7) * mm, "end": v(-7.98, -6.9) * mm});
            skLineSegment(sketch, "E368", {"start": v(-7.98, -6.9) * mm, "end": v(-8.1, -7.11) * mm});
            skLineSegment(sketch, "E369", {"start": v(-8.1, -7.11) * mm, "end": v(-8.2, -7.34) * mm});
            skLineSegment(sketch, "E370", {"start": v(-8.2, -7.34) * mm, "end": v(-8.06, -7.48) * mm});
            skLineSegment(sketch, "E371", {"start": v(-8.06, -7.48) * mm, "end": v(-7.93, -7.62) * mm});
            skLineSegment(sketch, "E372", {"start": v(-7.93, -7.62) * mm, "end": v(-7.7, -7.54) * mm});
            skLineSegment(sketch, "E373", {"start": v(-7.7, -7.54) * mm, "end": v(-7.47, -7.45) * mm});
            skLineSegment(sketch, "E374", {"start": v(-7.47, -7.45) * mm, "end": v(-7.26, -7.34) * mm});
            skLineSegment(sketch, "E375", {"start": v(-7.26, -7.34) * mm, "end": v(-7.06, -7.22) * mm});
            skLineSegment(sketch, "E376", {"start": v(-7.06, -7.22) * mm, "end": v(-6.88, -7.09) * mm});
            skLineSegment(sketch, "E377", {"start": v(-6.88, -7.09) * mm, "end": v(-6.72, -7.24) * mm});
            skLineSegment(sketch, "E378", {"start": v(-6.72, -7.24) * mm, "end": v(-6.55, -7.39) * mm});
            skLineSegment(sketch, "E379", {"start": v(-6.55, -7.39) * mm, "end": v(-6.68, -7.58) * mm});
            skLineSegment(sketch, "E380", {"start": v(-6.68, -7.58) * mm, "end": v(-6.78, -7.79) * mm});
            skLineSegment(sketch, "E381", {"start": v(-6.78, -7.79) * mm, "end": v(-6.87, -8) * mm});
            skLineSegment(sketch, "E382", {"start": v(-6.87, -8) * mm, "end": v(-6.94, -8.24) * mm});
            skLineSegment(sketch, "E383", {"start": v(-6.94, -8.24) * mm, "end": v(-7, -8.48) * mm});
            skLineSegment(sketch, "E384", {"start": v(-7, -8.48) * mm, "end": v(-6.86, -8.6) * mm});
            skLineSegment(sketch, "E385", {"start": v(-6.86, -8.6) * mm, "end": v(-6.7, -8.72) * mm});
            skLineSegment(sketch, "E386", {"start": v(-6.7, -8.72) * mm, "end": v(-6.49, -8.6) * mm});
            skLineSegment(sketch, "E387", {"start": v(-6.49, -8.6) * mm, "end": v(-6.28, -8.48) * mm});
            skLineSegment(sketch, "E388", {"start": v(-6.28, -8.48) * mm, "end": v(-6.08, -8.34) * mm});
            skLineSegment(sketch, "E389", {"start": v(-6.08, -8.34) * mm, "end": v(-5.9, -8.2) * mm});
            skLineSegment(sketch, "E390", {"start": v(-5.9, -8.2) * mm, "end": v(-5.75, -8.03) * mm});
            skLineSegment(sketch, "E391", {"start": v(-5.75, -8.03) * mm, "end": v(-5.56, -8.16) * mm});
            skLineSegment(sketch, "E392", {"start": v(-5.56, -8.16) * mm, "end": v(-5.38, -8.28) * mm});
            skLineSegment(sketch, "E393", {"start": v(-5.38, -8.28) * mm, "end": v(-5.47, -8.49) * mm});
            skLineSegment(sketch, "E394", {"start": v(-5.47, -8.49) * mm, "end": v(-5.54, -8.71) * mm});
            skLineSegment(sketch, "E395", {"start": v(-5.54, -8.71) * mm, "end": v(-5.6, -8.94) * mm});
            skLineSegment(sketch, "E396", {"start": v(-5.6, -8.94) * mm, "end": v(-5.64, -9.18) * mm});
            skLineSegment(sketch, "E397", {"start": v(-5.64, -9.18) * mm, "end": v(-5.66, -9.43) * mm});
            skLineSegment(sketch, "E398", {"start": v(-5.66, -9.43) * mm, "end": v(-5.5, -9.53) * mm});
            skLineSegment(sketch, "E399", {"start": v(-5.5, -9.53) * mm, "end": v(-5.33, -9.62) * mm});
            skLineSegment(sketch, "E400", {"start": v(-5.33, -9.62) * mm, "end": v(-5.13, -9.47) * mm});
            skLineSegment(sketch, "E401", {"start": v(-5.13, -9.47) * mm, "end": v(-4.95, -9.32) * mm});
            skLineSegment(sketch, "E402", {"start": v(-4.95, -9.32) * mm, "end": v(-4.77, -9.16) * mm});
            skLineSegment(sketch, "E403", {"start": v(-4.77, -9.16) * mm, "end": v(-4.62, -8.98) * mm});
            skLineSegment(sketch, "E404", {"start": v(-4.62, -8.98) * mm, "end": v(-4.48, -8.8) * mm});
            skLineSegment(sketch, "E405", {"start": v(-4.48, -8.8) * mm, "end": v(-4.28, -8.9) * mm});
            skLineSegment(sketch, "E406", {"start": v(-4.28, -8.9) * mm, "end": v(-4.08, -9) * mm});
            skLineSegment(sketch, "E407", {"start": v(-4.08, -9) * mm, "end": v(-4.15, -9.21) * mm});
            skLineSegment(sketch, "E408", {"start": v(-4.15, -9.21) * mm, "end": v(-4.18, -9.44) * mm});
            skLineSegment(sketch, "E409", {"start": v(-4.18, -9.44) * mm, "end": v(-4.2, -9.68) * mm});
            skLineSegment(sketch, "E410", {"start": v(-4.2, -9.68) * mm, "end": v(-4.2, -9.92) * mm});
            skLineSegment(sketch, "E411", {"start": v(-4.2, -9.92) * mm, "end": v(-4.2, -10.17) * mm});
            skLineSegment(sketch, "E412", {"start": v(-4.2, -10.17) * mm, "end": v(-4.02, -10.24) * mm});
            skLineSegment(sketch, "E413", {"start": v(-4.02, -10.24) * mm, "end": v(-3.84, -10.3) * mm});
            skLineSegment(sketch, "E414", {"start": v(-3.84, -10.3) * mm, "end": v(-3.66, -10.13) * mm});
            skLineSegment(sketch, "E415", {"start": v(-3.66, -10.13) * mm, "end": v(-3.5, -9.95) * mm});
            skLineSegment(sketch, "E416", {"start": v(-3.5, -9.95) * mm, "end": v(-3.35, -9.76) * mm});
            skLineSegment(sketch, "E417", {"start": v(-3.35, -9.76) * mm, "end": v(-3.23, -9.57) * mm});
            skLineSegment(sketch, "E418", {"start": v(-3.23, -9.57) * mm, "end": v(-3.12, -9.37) * mm});
            skLineSegment(sketch, "E419", {"start": v(-3.12, -9.37) * mm, "end": v(-2.91, -9.44) * mm});
            skLineSegment(sketch, "E420", {"start": v(-2.91, -9.44) * mm, "end": v(-2.7, -9.5) * mm});
            skLineSegment(sketch, "E421", {"start": v(-2.7, -9.5) * mm, "end": v(-2.73, -9.73) * mm});
            skLineSegment(sketch, "E422", {"start": v(-2.73, -9.73) * mm, "end": v(-2.73, -9.96) * mm});
            skLineSegment(sketch, "E423", {"start": v(-2.73, -9.96) * mm, "end": v(-2.71, -10.2) * mm});
            skLineSegment(sketch, "E424", {"start": v(-2.71, -10.2) * mm, "end": v(-2.68, -10.44) * mm});
            skLineSegment(sketch, "E425", {"start": v(-2.68, -10.44) * mm, "end": v(-2.63, -10.68) * mm});
            skLineSegment(sketch, "E426", {"start": v(-2.63, -10.68) * mm, "end": v(-2.45, -10.72) * mm});
            skLineSegment(sketch, "E427", {"start": v(-2.45, -10.72) * mm, "end": v(-2.26, -10.77) * mm});
            skLineSegment(sketch, "E428", {"start": v(-2.26, -10.77) * mm, "end": v(-2.11, -10.57) * mm});
            skLineSegment(sketch, "E429", {"start": v(-2.11, -10.57) * mm, "end": v(-1.98, -10.36) * mm});
            skLineSegment(sketch, "E430", {"start": v(-1.98, -10.36) * mm, "end": v(-1.86, -10.16) * mm});
            skLineSegment(sketch, "E431", {"start": v(-1.86, -10.16) * mm, "end": v(-1.76, -9.94) * mm});
            skLineSegment(sketch, "E432", {"start": v(-1.76, -9.94) * mm, "end": v(-1.7, -9.73) * mm});
            skLineSegment(sketch, "E433", {"start": v(-1.7, -9.73) * mm, "end": v(-1.47, -9.76) * mm});
            skLineSegment(sketch, "E434", {"start": v(-1.47, -9.76) * mm, "end": v(-1.25, -9.8) * mm});
            skLineSegment(sketch, "E435", {"start": v(-1.25, -9.8) * mm, "end": v(-1.25, -10.02) * mm});
            skLineSegment(sketch, "E436", {"start": v(-1.25, -10.02) * mm, "end": v(-1.21, -10.25) * mm});
            skLineSegment(sketch, "E437", {"start": v(-1.21, -10.25) * mm, "end": v(-1.16, -10.49) * mm});
            skLineSegment(sketch, "E438", {"start": v(-1.16, -10.49) * mm, "end": v(-1.1, -10.72) * mm});
            skLineSegment(sketch, "E439", {"start": v(-1.1, -10.72) * mm, "end": v(-1.01, -10.95) * mm});
            skLineSegment(sketch, "E440", {"start": v(-1.01, -10.95) * mm, "end": v(-0.82, -10.97) * mm});
            skLineSegment(sketch, "E441", {"start": v(-0.82, -10.97) * mm, "end": v(-0.63, -10.98) * mm});
            skLineSegment(sketch, "E442", {"start": v(-0.63, -10.98) * mm, "end": v(-0.51, -10.76) * mm});
            skLineSegment(sketch, "E443", {"start": v(-0.51, -10.76) * mm, "end": v(-0.41, -10.54) * mm});
            skLineSegment(sketch, "E444", {"start": v(-0.41, -10.54) * mm, "end": v(-0.33, -10.32) * mm});
            skLineSegment(sketch, "E445", {"start": v(-0.33, -10.32) * mm, "end": v(-0.26, -10.1) * mm});
            skLineSegment(sketch, "E446", {"start": v(-0.26, -10.1) * mm, "end": v(-0.22, -9.87) * mm});
            skLineSegment(sketch, "E447", {"start": v(-0.22, -9.87) * mm, "end": v(0, -9.88) * mm});
            skLineSegment(sketch, "E448", {"start": v(0, -9.88) * mm, "end": v(0.22, -9.87) * mm});
            skLineSegment(sketch, "E449", {"start": v(0.22, -9.87) * mm, "end": v(0.26, -10.1) * mm});
            skLineSegment(sketch, "E450", {"start": v(0.26, -10.1) * mm, "end": v(0.33, -10.32) * mm});
            skLineSegment(sketch, "E451", {"start": v(0.33, -10.32) * mm, "end": v(0.41, -10.54) * mm});
            skLineSegment(sketch, "E452", {"start": v(0.41, -10.54) * mm, "end": v(0.51, -10.76) * mm});
            skLineSegment(sketch, "E453", {"start": v(0.51, -10.76) * mm, "end": v(0.63, -10.98) * mm});
            skLineSegment(sketch, "E454", {"start": v(0.63, -10.98) * mm, "end": v(0.82, -10.97) * mm});
            skLineSegment(sketch, "E455", {"start": v(0.82, -10.97) * mm, "end": v(1.01, -10.95) * mm});
            skLineSegment(sketch, "E456", {"start": v(1.01, -10.95) * mm, "end": v(1.1, -10.72) * mm});
            skLineSegment(sketch, "E457", {"start": v(1.1, -10.72) * mm, "end": v(1.16, -10.49) * mm});
            skLineSegment(sketch, "E458", {"start": v(1.16, -10.49) * mm, "end": v(1.21, -10.25) * mm});
            skLineSegment(sketch, "E459", {"start": v(1.21, -10.25) * mm, "end": v(1.25, -10.02) * mm});
            skLineSegment(sketch, "E460", {"start": v(1.25, -10.02) * mm, "end": v(1.25, -9.8) * mm});
            skLineSegment(sketch, "E461", {"start": v(1.25, -9.8) * mm, "end": v(1.47, -9.76) * mm});
            skLineSegment(sketch, "E462", {"start": v(1.47, -9.76) * mm, "end": v(1.7, -9.73) * mm});
            skLineSegment(sketch, "E463", {"start": v(1.7, -9.73) * mm, "end": v(1.76, -9.94) * mm});
            skLineSegment(sketch, "E464", {"start": v(1.76, -9.94) * mm, "end": v(1.86, -10.16) * mm});
            skLineSegment(sketch, "E465", {"start": v(1.86, -10.16) * mm, "end": v(1.98, -10.36) * mm});
            skLineSegment(sketch, "E466", {"start": v(1.98, -10.36) * mm, "end": v(2.11, -10.57) * mm});
            skLineSegment(sketch, "E467", {"start": v(2.11, -10.57) * mm, "end": v(2.26, -10.77) * mm});
            skLineSegment(sketch, "E468", {"start": v(2.26, -10.77) * mm, "end": v(2.45, -10.72) * mm});
            skLineSegment(sketch, "E469", {"start": v(2.45, -10.72) * mm, "end": v(2.63, -10.68) * mm});
            skLineSegment(sketch, "E470", {"start": v(2.63, -10.68) * mm, "end": v(2.68, -10.44) * mm});
            skLineSegment(sketch, "E471", {"start": v(2.68, -10.44) * mm, "end": v(2.71, -10.2) * mm});
            skLineSegment(sketch, "E472", {"start": v(2.71, -10.2) * mm, "end": v(2.73, -9.96) * mm});
            skLineSegment(sketch, "E473", {"start": v(2.73, -9.96) * mm, "end": v(2.73, -9.73) * mm});
            skLineSegment(sketch, "E474", {"start": v(2.73, -9.73) * mm, "end": v(2.7, -9.5) * mm});
            skLineSegment(sketch, "E475", {"start": v(2.7, -9.5) * mm, "end": v(2.91, -9.44) * mm});
            skLineSegment(sketch, "E476", {"start": v(2.91, -9.44) * mm, "end": v(3.12, -9.37) * mm});
            skLineSegment(sketch, "E477", {"start": v(3.12, -9.37) * mm, "end": v(3.23, -9.57) * mm});
            skLineSegment(sketch, "E478", {"start": v(3.23, -9.57) * mm, "end": v(3.35, -9.76) * mm});
            skLineSegment(sketch, "E479", {"start": v(3.35, -9.76) * mm, "end": v(3.5, -9.95) * mm});
            skLineSegment(sketch, "E480", {"start": v(3.5, -9.95) * mm, "end": v(3.66, -10.13) * mm});
            skLineSegment(sketch, "E481", {"start": v(3.66, -10.13) * mm, "end": v(3.84, -10.3) * mm});
            skLineSegment(sketch, "E482", {"start": v(3.84, -10.3) * mm, "end": v(4.02, -10.24) * mm});
            skLineSegment(sketch, "E483", {"start": v(4.02, -10.24) * mm, "end": v(4.2, -10.17) * mm});
            skLineSegment(sketch, "E484", {"start": v(4.2, -10.17) * mm, "end": v(4.2, -9.92) * mm});
            skLineSegment(sketch, "E485", {"start": v(4.2, -9.92) * mm, "end": v(4.2, -9.68) * mm});
            skLineSegment(sketch, "E486", {"start": v(4.2, -9.68) * mm, "end": v(4.18, -9.44) * mm});
            skLineSegment(sketch, "E487", {"start": v(4.18, -9.44) * mm, "end": v(4.15, -9.21) * mm});
            skLineSegment(sketch, "E488", {"start": v(4.15, -9.21) * mm, "end": v(4.08, -9) * mm});
            skLineSegment(sketch, "E489", {"start": v(4.08, -9) * mm, "end": v(4.28, -8.9) * mm});
            skLineSegment(sketch, "E490", {"start": v(4.28, -8.9) * mm, "end": v(4.48, -8.8) * mm});
            skLineSegment(sketch, "E491", {"start": v(4.48, -8.8) * mm, "end": v(4.62, -8.98) * mm});
            skLineSegment(sketch, "E492", {"start": v(4.62, -8.98) * mm, "end": v(4.77, -9.16) * mm});
            skLineSegment(sketch, "E493", {"start": v(4.77, -9.16) * mm, "end": v(4.95, -9.32) * mm});
            skLineSegment(sketch, "E494", {"start": v(4.95, -9.32) * mm, "end": v(5.13, -9.47) * mm});
            skLineSegment(sketch, "E495", {"start": v(5.13, -9.47) * mm, "end": v(5.33, -9.62) * mm});
            skLineSegment(sketch, "E496", {"start": v(5.33, -9.62) * mm, "end": v(5.5, -9.53) * mm});
            skLineSegment(sketch, "E497", {"start": v(5.5, -9.53) * mm, "end": v(5.66, -9.43) * mm});
            skLineSegment(sketch, "E498", {"start": v(5.66, -9.43) * mm, "end": v(5.64, -9.18) * mm});
            skLineSegment(sketch, "E499", {"start": v(5.64, -9.18) * mm, "end": v(5.6, -8.94) * mm});
            skLineSegment(sketch, "E500", {"start": v(5.6, -8.94) * mm, "end": v(5.54, -8.71) * mm});
            skLineSegment(sketch, "E501", {"start": v(5.54, -8.71) * mm, "end": v(5.47, -8.49) * mm});
            skLineSegment(sketch, "E502", {"start": v(5.47, -8.49) * mm, "end": v(5.38, -8.28) * mm});
            skLineSegment(sketch, "E503", {"start": v(5.38, -8.28) * mm, "end": v(5.56, -8.16) * mm});
            skLineSegment(sketch, "E504", {"start": v(5.56, -8.16) * mm, "end": v(5.75, -8.03) * mm});
            skLineSegment(sketch, "E505", {"start": v(5.75, -8.03) * mm, "end": v(5.9, -8.2) * mm});
            skLineSegment(sketch, "E506", {"start": v(5.9, -8.2) * mm, "end": v(6.08, -8.34) * mm});
            skLineSegment(sketch, "E507", {"start": v(6.08, -8.34) * mm, "end": v(6.28, -8.48) * mm});
            skLineSegment(sketch, "E508", {"start": v(6.28, -8.48) * mm, "end": v(6.49, -8.6) * mm});
            skLineSegment(sketch, "E509", {"start": v(6.49, -8.6) * mm, "end": v(6.7, -8.72) * mm});
            skLineSegment(sketch, "E510", {"start": v(6.7, -8.72) * mm, "end": v(6.86, -8.6) * mm});
            skLineSegment(sketch, "E511", {"start": v(6.86, -8.6) * mm, "end": v(7, -8.48) * mm});
            skLineSegment(sketch, "E512", {"start": v(7, -8.48) * mm, "end": v(6.94, -8.24) * mm});
            skLineSegment(sketch, "E513", {"start": v(6.94, -8.24) * mm, "end": v(6.87, -8) * mm});
            skLineSegment(sketch, "E514", {"start": v(6.87, -8) * mm, "end": v(6.78, -7.79) * mm});
            skLineSegment(sketch, "E515", {"start": v(6.78, -7.79) * mm, "end": v(6.68, -7.58) * mm});
            skLineSegment(sketch, "E516", {"start": v(6.68, -7.58) * mm, "end": v(6.55, -7.39) * mm});
            skLineSegment(sketch, "E517", {"start": v(6.55, -7.39) * mm, "end": v(6.72, -7.24) * mm});
            skLineSegment(sketch, "E518", {"start": v(6.72, -7.24) * mm, "end": v(6.88, -7.09) * mm});
            skLineSegment(sketch, "E519", {"start": v(6.88, -7.09) * mm, "end": v(7.06, -7.22) * mm});
            skLineSegment(sketch, "E520", {"start": v(7.06, -7.22) * mm, "end": v(7.26, -7.34) * mm});
            skLineSegment(sketch, "E521", {"start": v(7.26, -7.34) * mm, "end": v(7.47, -7.45) * mm});
            skLineSegment(sketch, "E522", {"start": v(7.47, -7.45) * mm, "end": v(7.7, -7.54) * mm});
            skLineSegment(sketch, "E523", {"start": v(7.7, -7.54) * mm, "end": v(7.93, -7.62) * mm});
            skLineSegment(sketch, "E524", {"start": v(7.93, -7.62) * mm, "end": v(8.06, -7.48) * mm});
            skLineSegment(sketch, "E525", {"start": v(8.06, -7.48) * mm, "end": v(8.2, -7.34) * mm});
            skLineSegment(sketch, "E526", {"start": v(8.2, -7.34) * mm, "end": v(8.1, -7.11) * mm});
            skLineSegment(sketch, "E527", {"start": v(8.1, -7.11) * mm, "end": v(7.98, -6.9) * mm});
            skLineSegment(sketch, "E528", {"start": v(7.98, -6.9) * mm, "end": v(7.86, -6.7) * mm});
            skLineSegment(sketch, "E529", {"start": v(7.86, -6.7) * mm, "end": v(7.73, -6.5) * mm});
            skLineSegment(sketch, "E530", {"start": v(7.73, -6.5) * mm, "end": v(7.58, -6.33) * mm});
            skLineSegment(sketch, "E531", {"start": v(7.58, -6.33) * mm, "end": v(7.72, -6.16) * mm});
            skLineSegment(sketch, "E532", {"start": v(7.72, -6.16) * mm, "end": v(7.86, -5.98) * mm});
            skLineSegment(sketch, "E533", {"start": v(7.86, -5.98) * mm, "end": v(8.06, -6.1) * mm});
            skLineSegment(sketch, "E534", {"start": v(8.06, -6.1) * mm, "end": v(8.27, -6.18) * mm});
            skLineSegment(sketch, "E535", {"start": v(8.27, -6.18) * mm, "end": v(8.5, -6.25) * mm});
            skLineSegment(sketch, "E536", {"start": v(8.5, -6.25) * mm, "end": v(8.74, -6.3) * mm});
            skLineSegment(sketch, "E537", {"start": v(8.74, -6.3) * mm, "end": v(8.98, -6.35) * mm});
            skLineSegment(sketch, "E538", {"start": v(8.98, -6.35) * mm, "end": v(9.09, -6.2) * mm});
            skLineSegment(sketch, "E539", {"start": v(9.09, -6.2) * mm, "end": v(9.2, -6.04) * mm});
            skLineSegment(sketch, "E540", {"start": v(9.2, -6.04) * mm, "end": v(9.06, -5.83) * mm});
            skLineSegment(sketch, "E541", {"start": v(9.06, -5.83) * mm, "end": v(8.92, -5.63) * mm});
            skLineSegment(sketch, "E542", {"start": v(8.92, -5.63) * mm, "end": v(8.77, -5.44) * mm});
            skLineSegment(sketch, "E543", {"start": v(8.77, -5.44) * mm, "end": v(8.61, -5.27) * mm});
            skLineSegment(sketch, "E544", {"start": v(8.61, -5.27) * mm, "end": v(8.44, -5.13) * mm});
            skLineSegment(sketch, "E545", {"start": v(8.44, -5.13) * mm, "end": v(8.55, -4.94) * mm});
            skLineSegment(sketch, "E546", {"start": v(8.55, -4.94) * mm, "end": v(8.66, -4.74) * mm});
            skLineSegment(sketch, "E547", {"start": v(8.66, -4.74) * mm, "end": v(8.87, -4.82) * mm});
            skLineSegment(sketch, "E548", {"start": v(8.87, -4.82) * mm, "end": v(9.1, -4.88) * mm});
            skLineSegment(sketch, "E549", {"start": v(9.1, -4.88) * mm, "end": v(9.34, -4.91) * mm});
            skLineSegment(sketch, "E550", {"start": v(9.34, -4.91) * mm, "end": v(9.58, -4.94) * mm});
            skLineSegment(sketch, "E551", {"start": v(9.58, -4.94) * mm, "end": v(9.83, -4.94) * mm});
            skLineSegment(sketch, "E552", {"start": v(9.83, -4.94) * mm, "end": v(9.91, -4.77) * mm});
            skLineSegment(sketch, "E553", {"start": v(9.91, -4.77) * mm, "end": v(10, -4.6) * mm});
            skLineSegment(sketch, "E554", {"start": v(10, -4.6) * mm, "end": v(9.83, -4.41) * mm});
            skLineSegment(sketch, "E555", {"start": v(9.83, -4.41) * mm, "end": v(9.66, -4.24) * mm});
            skLineSegment(sketch, "E556", {"start": v(9.66, -4.24) * mm, "end": v(9.49, -4.08) * mm});
            skLineSegment(sketch, "E557", {"start": v(9.49, -4.08) * mm, "end": v(9.3, -3.93) * mm});
            skLineSegment(sketch, "E558", {"start": v(9.3, -3.93) * mm, "end": v(9.1, -3.81) * mm});
            skLineSegment(sketch, "E559", {"start": v(9.1, -3.81) * mm, "end": v(9.2, -3.6) * mm});
            skLineSegment(sketch, "E560", {"start": v(9.2, -3.6) * mm, "end": v(9.27, -3.4) * mm});
            skLineSegment(sketch, "E561", {"start": v(9.27, -3.4) * mm, "end": v(9.5, -3.45) * mm});
            skLineSegment(sketch, "E562", {"start": v(9.5, -3.45) * mm, "end": v(9.73, -3.47) * mm});
            skLineSegment(sketch, "E563", {"start": v(9.73, -3.47) * mm, "end": v(9.96, -3.47) * mm});
            skLineSegment(sketch, "E564", {"start": v(9.96, -3.47) * mm, "end": v(10.2, -3.45) * mm});
            skLineSegment(sketch, "E565", {"start": v(10.2, -3.45) * mm, "end": v(10.45, -3.42) * mm});
            skLineSegment(sketch, "E566", {"start": v(10.45, -3.42) * mm, "end": v(10.51, -3.24) * mm});
            skLineSegment(sketch, "E567", {"start": v(10.51, -3.24) * mm, "end": v(10.57, -3.06) * mm});
            skLineSegment(sketch, "E568", {"start": v(10.57, -3.06) * mm, "end": v(10.38, -2.9) * mm});
            skLineSegment(sketch, "E569", {"start": v(10.38, -2.9) * mm, "end": v(10.19, -2.75) * mm});
            skLineSegment(sketch, "E570", {"start": v(10.19, -2.75) * mm, "end": v(9.99, -2.62) * mm});
            skLineSegment(sketch, "E571", {"start": v(9.99, -2.62) * mm, "end": v(9.79, -2.5) * mm});
            skLineSegment(sketch, "E572", {"start": v(9.79, -2.5) * mm, "end": v(9.58, -2.41) * mm});
            skLineSegment(sketch, "E573", {"start": v(9.58, -2.41) * mm, "end": v(9.63, -2.2) * mm});
            skLineSegment(sketch, "E574", {"start": v(9.63, -2.2) * mm, "end": v(9.67, -1.98) * mm});
            skLineSegment(sketch, "E575", {"start": v(9.67, -1.98) * mm, "end": v(9.9, -2) * mm});
            skLineSegment(sketch, "E576", {"start": v(9.9, -2) * mm, "end": v(10.13, -1.98) * mm});
            skLineSegment(sketch, "E577", {"start": v(10.13, -1.98) * mm, "end": v(10.37, -1.94) * mm});
            skLineSegment(sketch, "E578", {"start": v(10.37, -1.94) * mm, "end": v(10.6, -1.9) * mm});
            skLineSegment(sketch, "E579", {"start": v(10.6, -1.9) * mm, "end": v(10.85, -1.83) * mm});
            skLineSegment(sketch, "E580", {"start": v(10.85, -1.83) * mm, "end": v(10.88, -1.64) * mm});
            skLineSegment(sketch, "E581", {"start": v(10.88, -1.64) * mm, "end": v(10.9, -1.45) * mm});
            skLineSegment(sketch, "E582", {"start": v(10.9, -1.45) * mm, "end": v(10.7, -1.32) * mm});
            skLineSegment(sketch, "E583", {"start": v(10.7, -1.32) * mm, "end": v(10.48, -1.2) * mm});
            skLineSegment(sketch, "E584", {"start": v(10.48, -1.2) * mm, "end": v(10.27, -1.1) * mm});
            skLineSegment(sketch, "E585", {"start": v(10.27, -1.1) * mm, "end": v(10.05, -1.02) * mm});
            skLineSegment(sketch, "E586", {"start": v(10.05, -1.02) * mm, "end": v(9.83, -0.96) * mm});
            skLineSegment(sketch, "E587", {"start": v(9.85, -0.74) * mm, "end": v(9.83, -0.96) * mm});
            skSolve(sketch);
        }
        {
            var Q0;
            Q0=makeQuery(id+"F0.imprint","IMPRINT",FACE,{"disambiguationData":[TD([[makeQuery(id+"F0.imprint","IMPRINT",EDGE,{"derivedFrom":sQuery(id+"F0.wireOp",EDGE,"E0")}),1.0]])]});
            extrude(context, id + "F1", {"entities" : qUnion([Q0]), "depth" : 2 * mm});
        }
        {
            var Q0;
            Q0=makeQuery(id+"F1.opExtrude","CAP_FACE",FACE,{"disambiguationData":[OSD([sQuery(id+"F0.wireOp",EDGE,"E0"),sQuery(id+"F0.wireOp",EDGE,"E1"),sQuery(id+"F0.wireOp",EDGE,"E2"),sQuery(id+"F0.wireOp",EDGE,"E3"),sQuery(id+"F0.wireOp",EDGE,"E4"),sQuery(id+"F0.wireOp",EDGE,"E5"),sQuery(id+"F0.wireOp",EDGE,"E6"),sQuery(id+"F0.wireOp",EDGE,"E7"),sQuery(id+"F0.wireOp",EDGE,"E8"),sQuery(id+"F0.wireOp",EDGE,"E9"),sQuery(id+"F0.wireOp",EDGE,"E10"),sQuery(id+"F0.wireOp",EDGE,"E11"),sQuery(id+"F0.wireOp",EDGE,"E12"),sQuery(id+"F0.wireOp",EDGE,"E13"),sQuery(id+"F0.wireOp",EDGE,"E14"),sQuery(id+"F0.wireOp",EDGE,"E15"),sQuery(id+"F0.wireOp",EDGE,"E16"),sQuery(id+"F0.wireOp",EDGE,"E17"),sQuery(id+"F0.wireOp",EDGE,"E18"),sQuery(id+"F0.wireOp",EDGE,"E19"),sQuery(id+"F0.wireOp",EDGE,"E20"),sQuery(id+"F0.wireOp",EDGE,"E21"),sQuery(id+"F0.wireOp",EDGE,"E22"),sQuery(id+"F0.wireOp",EDGE,"E23"),sQuery(id+"F0.wireOp",EDGE,"E24"),sQuery(id+"F0.wireOp",EDGE,"E25"),sQuery(id+"F0.wireOp",EDGE,"E26"),sQuery(id+"F0.wireOp",EDGE,"E27"),sQuery(id+"F0.wireOp",EDGE,"E28"),sQuery(id+"F0.wireOp",EDGE,"E29"),sQuery(id+"F0.wireOp",EDGE,"E30"),sQuery(id+"F0.wireOp",EDGE,"E31"),sQuery(id+"F0.wireOp",EDGE,"E32"),sQuery(id+"F0.wireOp",EDGE,"E33"),sQuery(id+"F0.wireOp",EDGE,"E34"),sQuery(id+"F0.wireOp",EDGE,"E35"),sQuery(id+"F0.wireOp",EDGE,"E36"),sQuery(id+"F0.wireOp",EDGE,"E37"),sQuery(id+"F0.wireOp",EDGE,"E38"),sQuery(id+"F0.wireOp",EDGE,"E39"),sQuery(id+"F0.wireOp",EDGE,"E40"),sQuery(id+"F0.wireOp",EDGE,"E41"),sQuery(id+"F0.wireOp",EDGE,"E42"),sQuery(id+"F0.wireOp",EDGE,"E43"),sQuery(id+"F0.wireOp",EDGE,"E44"),sQuery(id+"F0.wireOp",EDGE,"E45"),sQuery(id+"F0.wireOp",EDGE,"E46"),sQuery(id+"F0.wireOp",EDGE,"E47"),sQuery(id+"F0.wireOp",EDGE,"E48"),sQuery(id+"F0.wireOp",EDGE,"E49"),sQuery(id+"F0.wireOp",EDGE,"E50"),sQuery(id+"F0.wireOp",EDGE,"E51"),sQuery(id+"F0.wireOp",EDGE,"E52"),sQuery(id+"F0.wireOp",EDGE,"E53"),sQuery(id+"F0.wireOp",EDGE,"E54"),sQuery(id+"F0.wireOp",EDGE,"E55"),sQuery(id+"F0.wireOp",EDGE,"E56"),sQuery(id+"F0.wireOp",EDGE,"E57"),sQuery(id+"F0.wireOp",EDGE,"E58"),sQuery(id+"F0.wireOp",EDGE,"E59"),sQuery(id+"F0.wireOp",EDGE,"E60"),sQuery(id+"F0.wireOp",EDGE,"E61"),sQuery(id+"F0.wireOp",EDGE,"E62"),sQuery(id+"F0.wireOp",EDGE,"E63"),sQuery(id+"F0.wireOp",EDGE,"E64"),sQuery(id+"F0.wireOp",EDGE,"E65"),sQuery(id+"F0.wireOp",EDGE,"E66"),sQuery(id+"F0.wireOp",EDGE,"E67"),sQuery(id+"F0.wireOp",EDGE,"E68"),sQuery(id+"F0.wireOp",EDGE,"E69"),sQuery(id+"F0.wireOp",EDGE,"E70"),sQuery(id+"F0.wireOp",EDGE,"E71"),sQuery(id+"F0.wireOp",EDGE,"E72"),sQuery(id+"F0.wireOp",EDGE,"E73"),sQuery(id+"F0.wireOp",EDGE,"E74"),sQuery(id+"F0.wireOp",EDGE,"E75"),sQuery(id+"F0.wireOp",EDGE,"E76"),sQuery(id+"F0.wireOp",EDGE,"E77"),sQuery(id+"F0.wireOp",EDGE,"E78"),sQuery(id+"F0.wireOp",EDGE,"E79"),sQuery(id+"F0.wireOp",EDGE,"E80"),sQuery(id+"F0.wireOp",EDGE,"E81"),sQuery(id+"F0.wireOp",EDGE,"E82"),sQuery(id+"F0.wireOp",EDGE,"E83"),sQuery(id+"F0.wireOp",EDGE,"E84"),sQuery(id+"F0.wireOp",EDGE,"E85"),sQuery(id+"F0.wireOp",EDGE,"E86"),sQuery(id+"F0.wireOp",EDGE,"E87"),sQuery(id+"F0.wireOp",EDGE,"E88"),sQuery(id+"F0.wireOp",EDGE,"E89"),sQuery(id+"F0.wireOp",EDGE,"E90"),sQuery(id+"F0.wireOp",EDGE,"E91"),sQuery(id+"F0.wireOp",EDGE,"E92"),sQuery(id+"F0.wireOp",EDGE,"E93"),sQuery(id+"F0.wireOp",EDGE,"E94"),sQuery(id+"F0.wireOp",EDGE,"E95"),sQuery(id+"F0.wireOp",EDGE,"E96"),sQuery(id+"F0.wireOp",EDGE,"E97"),sQuery(id+"F0.wireOp",EDGE,"E98"),sQuery(id+"F0.wireOp",EDGE,"E99"),sQuery(id+"F0.wireOp",EDGE,"E100"),sQuery(id+"F0.wireOp",EDGE,"E101"),sQuery(id+"F0.wireOp",EDGE,"E102"),sQuery(id+"F0.wireOp",EDGE,"E103"),sQuery(id+"F0.wireOp",EDGE,"E104"),sQuery(id+"F0.wireOp",EDGE,"E105"),sQuery(id+"F0.wireOp",EDGE,"E106"),sQuery(id+"F0.wireOp",EDGE,"E107"),sQuery(id+"F0.wireOp",EDGE,"E108"),sQuery(id+"F0.wireOp",EDGE,"E109"),sQuery(id+"F0.wireOp",EDGE,"E110"),sQuery(id+"F0.wireOp",EDGE,"E111"),sQuery(id+"F0.wireOp",EDGE,"E112"),sQuery(id+"F0.wireOp",EDGE,"E113"),sQuery(id+"F0.wireOp",EDGE,"E114"),sQuery(id+"F0.wireOp",EDGE,"E115"),sQuery(id+"F0.wireOp",EDGE,"E116"),sQuery(id+"F0.wireOp",EDGE,"E117"),sQuery(id+"F0.wireOp",EDGE,"E118"),sQuery(id+"F0.wireOp",EDGE,"E119"),sQuery(id+"F0.wireOp",EDGE,"E120"),sQuery(id+"F0.wireOp",EDGE,"E121"),sQuery(id+"F0.wireOp",EDGE,"E122"),sQuery(id+"F0.wireOp",EDGE,"E123"),sQuery(id+"F0.wireOp",EDGE,"E124"),sQuery(id+"F0.wireOp",EDGE,"E125"),sQuery(id+"F0.wireOp",EDGE,"E126"),sQuery(id+"F0.wireOp",EDGE,"E127"),sQuery(id+"F0.wireOp",EDGE,"E128"),sQuery(id+"F0.wireOp",EDGE,"E129"),sQuery(id+"F0.wireOp",EDGE,"E130"),sQuery(id+"F0.wireOp",EDGE,"E131"),sQuery(id+"F0.wireOp",EDGE,"E132"),sQuery(id+"F0.wireOp",EDGE,"E133"),sQuery(id+"F0.wireOp",EDGE,"E134"),sQuery(id+"F0.wireOp",EDGE,"E135"),sQuery(id+"F0.wireOp",EDGE,"E136"),sQuery(id+"F0.wireOp",EDGE,"E137"),sQuery(id+"F0.wireOp",EDGE,"E138"),sQuery(id+"F0.wireOp",EDGE,"E139"),sQuery(id+"F0.wireOp",EDGE,"E140"),sQuery(id+"F0.wireOp",EDGE,"E141"),sQuery(id+"F0.wireOp",EDGE,"E142"),sQuery(id+"F0.wireOp",EDGE,"E143"),sQuery(id+"F0.wireOp",EDGE,"E144"),sQuery(id+"F0.wireOp",EDGE,"E145"),sQuery(id+"F0.wireOp",EDGE,"E146"),sQuery(id+"F0.wireOp",EDGE,"E147"),sQuery(id+"F0.wireOp",EDGE,"E148"),sQuery(id+"F0.wireOp",EDGE,"E149"),sQuery(id+"F0.wireOp",EDGE,"E150"),sQuery(id+"F0.wireOp",EDGE,"E151"),sQuery(id+"F0.wireOp",EDGE,"E152"),sQuery(id+"F0.wireOp",EDGE,"E153"),sQuery(id+"F0.wireOp",EDGE,"E154"),sQuery(id+"F0.wireOp",EDGE,"E155"),sQuery(id+"F0.wireOp",EDGE,"E156"),sQuery(id+"F0.wireOp",EDGE,"E157"),sQuery(id+"F0.wireOp",EDGE,"E158"),sQuery(id+"F0.wireOp",EDGE,"E159"),sQuery(id+"F0.wireOp",EDGE,"E160"),sQuery(id+"F0.wireOp",EDGE,"E161"),sQuery(id+"F0.wireOp",EDGE,"E162"),sQuery(id+"F0.wireOp",EDGE,"E163"),sQuery(id+"F0.wireOp",EDGE,"E164"),sQuery(id+"F0.wireOp",EDGE,"E165"),sQuery(id+"F0.wireOp",EDGE,"E166"),sQuery(id+"F0.wireOp",EDGE,"E167"),sQuery(id+"F0.wireOp",EDGE,"E168"),sQuery(id+"F0.wireOp",EDGE,"E169"),sQuery(id+"F0.wireOp",EDGE,"E170"),sQuery(id+"F0.wireOp",EDGE,"E171"),sQuery(id+"F0.wireOp",EDGE,"E172"),sQuery(id+"F0.wireOp",EDGE,"E173"),sQuery(id+"F0.wireOp",EDGE,"E174"),sQuery(id+"F0.wireOp",EDGE,"E175"),sQuery(id+"F0.wireOp",EDGE,"E176"),sQuery(id+"F0.wireOp",EDGE,"E177"),sQuery(id+"F0.wireOp",EDGE,"E178"),sQuery(id+"F0.wireOp",EDGE,"E179"),sQuery(id+"F0.wireOp",EDGE,"E180"),sQuery(id+"F0.wireOp",EDGE,"E181"),sQuery(id+"F0.wireOp",EDGE,"E182"),sQuery(id+"F0.wireOp",EDGE,"E183"),sQuery(id+"F0.wireOp",EDGE,"E184"),sQuery(id+"F0.wireOp",EDGE,"E185"),sQuery(id+"F0.wireOp",EDGE,"E186"),sQuery(id+"F0.wireOp",EDGE,"E187"),sQuery(id+"F0.wireOp",EDGE,"E188"),sQuery(id+"F0.wireOp",EDGE,"E189"),sQuery(id+"F0.wireOp",EDGE,"E190"),sQuery(id+"F0.wireOp",EDGE,"E191"),sQuery(id+"F0.wireOp",EDGE,"E192"),sQuery(id+"F0.wireOp",EDGE,"E193"),sQuery(id+"F0.wireOp",EDGE,"E194"),sQuery(id+"F0.wireOp",EDGE,"E195"),sQuery(id+"F0.wireOp",EDGE,"E196"),sQuery(id+"F0.wireOp",EDGE,"E197"),sQuery(id+"F0.wireOp",EDGE,"E198"),sQuery(id+"F0.wireOp",EDGE,"E199"),sQuery(id+"F0.wireOp",EDGE,"E200"),sQuery(id+"F0.wireOp",EDGE,"E201"),sQuery(id+"F0.wireOp",EDGE,"E202"),sQuery(id+"F0.wireOp",EDGE,"E203"),sQuery(id+"F0.wireOp",EDGE,"E204"),sQuery(id+"F0.wireOp",EDGE,"E205"),sQuery(id+"F0.wireOp",EDGE,"E206"),sQuery(id+"F0.wireOp",EDGE,"E207"),sQuery(id+"F0.wireOp",EDGE,"E208"),sQuery(id+"F0.wireOp",EDGE,"E209"),sQuery(id+"F0.wireOp",EDGE,"E210"),sQuery(id+"F0.wireOp",EDGE,"E211"),sQuery(id+"F0.wireOp",EDGE,"E212"),sQuery(id+"F0.wireOp",EDGE,"E213"),sQuery(id+"F0.wireOp",EDGE,"E214"),sQuery(id+"F0.wireOp",EDGE,"E215"),sQuery(id+"F0.wireOp",EDGE,"E216"),sQuery(id+"F0.wireOp",EDGE,"E217"),sQuery(id+"F0.wireOp",EDGE,"E218"),sQuery(id+"F0.wireOp",EDGE,"E219"),sQuery(id+"F0.wireOp",EDGE,"E220"),sQuery(id+"F0.wireOp",EDGE,"E221"),sQuery(id+"F0.wireOp",EDGE,"E222"),sQuery(id+"F0.wireOp",EDGE,"E223"),sQuery(id+"F0.wireOp",EDGE,"E224"),sQuery(id+"F0.wireOp",EDGE,"E225"),sQuery(id+"F0.wireOp",EDGE,"E226"),sQuery(id+"F0.wireOp",EDGE,"E227"),sQuery(id+"F0.wireOp",EDGE,"E228"),sQuery(id+"F0.wireOp",EDGE,"E229"),sQuery(id+"F0.wireOp",EDGE,"E230"),sQuery(id+"F0.wireOp",EDGE,"E231"),sQuery(id+"F0.wireOp",EDGE,"E232"),sQuery(id+"F0.wireOp",EDGE,"E233"),sQuery(id+"F0.wireOp",EDGE,"E234"),sQuery(id+"F0.wireOp",EDGE,"E235"),sQuery(id+"F0.wireOp",EDGE,"E236"),sQuery(id+"F0.wireOp",EDGE,"E237"),sQuery(id+"F0.wireOp",EDGE,"E238"),sQuery(id+"F0.wireOp",EDGE,"E239"),sQuery(id+"F0.wireOp",EDGE,"E240"),sQuery(id+"F0.wireOp",EDGE,"E241"),sQuery(id+"F0.wireOp",EDGE,"E242"),sQuery(id+"F0.wireOp",EDGE,"E243"),sQuery(id+"F0.wireOp",EDGE,"E244"),sQuery(id+"F0.wireOp",EDGE,"E245"),sQuery(id+"F0.wireOp",EDGE,"E246"),sQuery(id+"F0.wireOp",EDGE,"E247"),sQuery(id+"F0.wireOp",EDGE,"E248"),sQuery(id+"F0.wireOp",EDGE,"E249"),sQuery(id+"F0.wireOp",EDGE,"E250"),sQuery(id+"F0.wireOp",EDGE,"E251"),sQuery(id+"F0.wireOp",EDGE,"E252"),sQuery(id+"F0.wireOp",EDGE,"E253"),sQuery(id+"F0.wireOp",EDGE,"E254"),sQuery(id+"F0.wireOp",EDGE,"E255"),sQuery(id+"F0.wireOp",EDGE,"E256"),sQuery(id+"F0.wireOp",EDGE,"E257"),sQuery(id+"F0.wireOp",EDGE,"E258"),sQuery(id+"F0.wireOp",EDGE,"E259"),sQuery(id+"F0.wireOp",EDGE,"E260"),sQuery(id+"F0.wireOp",EDGE,"E261"),sQuery(id+"F0.wireOp",EDGE,"E262"),sQuery(id+"F0.wireOp",EDGE,"E263"),sQuery(id+"F0.wireOp",EDGE,"E264"),sQuery(id+"F0.wireOp",EDGE,"E265"),sQuery(id+"F0.wireOp",EDGE,"E266"),sQuery(id+"F0.wireOp",EDGE,"E267"),sQuery(id+"F0.wireOp",EDGE,"E268"),sQuery(id+"F0.wireOp",EDGE,"E269"),sQuery(id+"F0.wireOp",EDGE,"E270"),sQuery(id+"F0.wireOp",EDGE,"E271"),sQuery(id+"F0.wireOp",EDGE,"E272"),sQuery(id+"F0.wireOp",EDGE,"E273"),sQuery(id+"F0.wireOp",EDGE,"E274"),sQuery(id+"F0.wireOp",EDGE,"E275"),sQuery(id+"F0.wireOp",EDGE,"E276"),sQuery(id+"F0.wireOp",EDGE,"E277"),sQuery(id+"F0.wireOp",EDGE,"E278"),sQuery(id+"F0.wireOp",EDGE,"E279"),sQuery(id+"F0.wireOp",EDGE,"E280"),sQuery(id+"F0.wireOp",EDGE,"E281"),sQuery(id+"F0.wireOp",EDGE,"E282"),sQuery(id+"F0.wireOp",EDGE,"E283"),sQuery(id+"F0.wireOp",EDGE,"E284"),sQuery(id+"F0.wireOp",EDGE,"E285"),sQuery(id+"F0.wireOp",EDGE,"E286"),sQuery(id+"F0.wireOp",EDGE,"E287"),sQuery(id+"F0.wireOp",EDGE,"E288"),sQuery(id+"F0.wireOp",EDGE,"E289"),sQuery(id+"F0.wireOp",EDGE,"E290"),sQuery(id+"F0.wireOp",EDGE,"E291"),sQuery(id+"F0.wireOp",EDGE,"E292"),sQuery(id+"F0.wireOp",EDGE,"E293"),sQuery(id+"F0.wireOp",EDGE,"E294"),sQuery(id+"F0.wireOp",EDGE,"E295"),sQuery(id+"F0.wireOp",EDGE,"E296"),sQuery(id+"F0.wireOp",EDGE,"E297"),sQuery(id+"F0.wireOp",EDGE,"E298"),sQuery(id+"F0.wireOp",EDGE,"E299"),sQuery(id+"F0.wireOp",EDGE,"E300"),sQuery(id+"F0.wireOp",EDGE,"E301"),sQuery(id+"F0.wireOp",EDGE,"E302"),sQuery(id+"F0.wireOp",EDGE,"E303"),sQuery(id+"F0.wireOp",EDGE,"E304"),sQuery(id+"F0.wireOp",EDGE,"E305"),sQuery(id+"F0.wireOp",EDGE,"E306"),sQuery(id+"F0.wireOp",EDGE,"E307"),sQuery(id+"F0.wireOp",EDGE,"E308"),sQuery(id+"F0.wireOp",EDGE,"E309"),sQuery(id+"F0.wireOp",EDGE,"E310"),sQuery(id+"F0.wireOp",EDGE,"E311"),sQuery(id+"F0.wireOp",EDGE,"E312"),sQuery(id+"F0.wireOp",EDGE,"E313"),sQuery(id+"F0.wireOp",EDGE,"E314"),sQuery(id+"F0.wireOp",EDGE,"E315"),sQuery(id+"F0.wireOp",EDGE,"E316"),sQuery(id+"F0.wireOp",EDGE,"E317"),sQuery(id+"F0.wireOp",EDGE,"E318"),sQuery(id+"F0.wireOp",EDGE,"E319"),sQuery(id+"F0.wireOp",EDGE,"E320"),sQuery(id+"F0.wireOp",EDGE,"E321"),sQuery(id+"F0.wireOp",EDGE,"E322"),sQuery(id+"F0.wireOp",EDGE,"E323"),sQuery(id+"F0.wireOp",EDGE,"E324"),sQuery(id+"F0.wireOp",EDGE,"E325"),sQuery(id+"F0.wireOp",EDGE,"E326"),sQuery(id+"F0.wireOp",EDGE,"E327"),sQuery(id+"F0.wireOp",EDGE,"E328"),sQuery(id+"F0.wireOp",EDGE,"E329"),sQuery(id+"F0.wireOp",EDGE,"E330"),sQuery(id+"F0.wireOp",EDGE,"E331"),sQuery(id+"F0.wireOp",EDGE,"E332"),sQuery(id+"F0.wireOp",EDGE,"E333"),sQuery(id+"F0.wireOp",EDGE,"E334"),sQuery(id+"F0.wireOp",EDGE,"E335"),sQuery(id+"F0.wireOp",EDGE,"E336"),sQuery(id+"F0.wireOp",EDGE,"E337"),sQuery(id+"F0.wireOp",EDGE,"E338"),sQuery(id+"F0.wireOp",EDGE,"E339"),sQuery(id+"F0.wireOp",EDGE,"E340"),sQuery(id+"F0.wireOp",EDGE,"E341"),sQuery(id+"F0.wireOp",EDGE,"E342"),sQuery(id+"F0.wireOp",EDGE,"E343"),sQuery(id+"F0.wireOp",EDGE,"E344"),sQuery(id+"F0.wireOp",EDGE,"E345"),sQuery(id+"F0.wireOp",EDGE,"E346"),sQuery(id+"F0.wireOp",EDGE,"E347"),sQuery(id+"F0.wireOp",EDGE,"E348"),sQuery(id+"F0.wireOp",EDGE,"E349"),sQuery(id+"F0.wireOp",EDGE,"E350"),sQuery(id+"F0.wireOp",EDGE,"E351"),sQuery(id+"F0.wireOp",EDGE,"E352"),sQuery(id+"F0.wireOp",EDGE,"E353"),sQuery(id+"F0.wireOp",EDGE,"E354"),sQuery(id+"F0.wireOp",EDGE,"E355"),sQuery(id+"F0.wireOp",EDGE,"E356"),sQuery(id+"F0.wireOp",EDGE,"E357"),sQuery(id+"F0.wireOp",EDGE,"E358"),sQuery(id+"F0.wireOp",EDGE,"E359"),sQuery(id+"F0.wireOp",EDGE,"E360"),sQuery(id+"F0.wireOp",EDGE,"E361"),sQuery(id+"F0.wireOp",EDGE,"E362"),sQuery(id+"F0.wireOp",EDGE,"E363"),sQuery(id+"F0.wireOp",EDGE,"E364"),sQuery(id+"F0.wireOp",EDGE,"E365"),sQuery(id+"F0.wireOp",EDGE,"E366"),sQuery(id+"F0.wireOp",EDGE,"E367"),sQuery(id+"F0.wireOp",EDGE,"E368"),sQuery(id+"F0.wireOp",EDGE,"E369"),sQuery(id+"F0.wireOp",EDGE,"E370"),sQuery(id+"F0.wireOp",EDGE,"E371"),sQuery(id+"F0.wireOp",EDGE,"E372"),sQuery(id+"F0.wireOp",EDGE,"E373"),sQuery(id+"F0.wireOp",EDGE,"E374"),sQuery(id+"F0.wireOp",EDGE,"E375"),sQuery(id+"F0.wireOp",EDGE,"E376"),sQuery(id+"F0.wireOp",EDGE,"E377"),sQuery(id+"F0.wireOp",EDGE,"E378"),sQuery(id+"F0.wireOp",EDGE,"E379"),sQuery(id+"F0.wireOp",EDGE,"E380"),sQuery(id+"F0.wireOp",EDGE,"E381"),sQuery(id+"F0.wireOp",EDGE,"E382"),sQuery(id+"F0.wireOp",EDGE,"E383"),sQuery(id+"F0.wireOp",EDGE,"E384"),sQuery(id+"F0.wireOp",EDGE,"E385"),sQuery(id+"F0.wireOp",EDGE,"E386"),sQuery(id+"F0.wireOp",EDGE,"E387"),sQuery(id+"F0.wireOp",EDGE,"E388"),sQuery(id+"F0.wireOp",EDGE,"E389"),sQuery(id+"F0.wireOp",EDGE,"E390"),sQuery(id+"F0.wireOp",EDGE,"E391"),sQuery(id+"F0.wireOp",EDGE,"E392"),sQuery(id+"F0.wireOp",EDGE,"E393"),sQuery(id+"F0.wireOp",EDGE,"E394"),sQuery(id+"F0.wireOp",EDGE,"E395"),sQuery(id+"F0.wireOp",EDGE,"E396"),sQuery(id+"F0.wireOp",EDGE,"E397"),sQuery(id+"F0.wireOp",EDGE,"E398"),sQuery(id+"F0.wireOp",EDGE,"E399"),sQuery(id+"F0.wireOp",EDGE,"E400"),sQuery(id+"F0.wireOp",EDGE,"E401"),sQuery(id+"F0.wireOp",EDGE,"E402"),sQuery(id+"F0.wireOp",EDGE,"E403"),sQuery(id+"F0.wireOp",EDGE,"E404"),sQuery(id+"F0.wireOp",EDGE,"E405"),sQuery(id+"F0.wireOp",EDGE,"E406"),sQuery(id+"F0.wireOp",EDGE,"E407"),sQuery(id+"F0.wireOp",EDGE,"E408"),sQuery(id+"F0.wireOp",EDGE,"E409"),sQuery(id+"F0.wireOp",EDGE,"E410"),sQuery(id+"F0.wireOp",EDGE,"E411"),sQuery(id+"F0.wireOp",EDGE,"E412"),sQuery(id+"F0.wireOp",EDGE,"E413"),sQuery(id+"F0.wireOp",EDGE,"E414"),sQuery(id+"F0.wireOp",EDGE,"E415"),sQuery(id+"F0.wireOp",EDGE,"E416"),sQuery(id+"F0.wireOp",EDGE,"E417"),sQuery(id+"F0.wireOp",EDGE,"E418"),sQuery(id+"F0.wireOp",EDGE,"E419"),sQuery(id+"F0.wireOp",EDGE,"E420"),sQuery(id+"F0.wireOp",EDGE,"E421"),sQuery(id+"F0.wireOp",EDGE,"E422"),sQuery(id+"F0.wireOp",EDGE,"E423"),sQuery(id+"F0.wireOp",EDGE,"E424"),sQuery(id+"F0.wireOp",EDGE,"E425"),sQuery(id+"F0.wireOp",EDGE,"E426"),sQuery(id+"F0.wireOp",EDGE,"E427"),sQuery(id+"F0.wireOp",EDGE,"E428"),sQuery(id+"F0.wireOp",EDGE,"E429"),sQuery(id+"F0.wireOp",EDGE,"E430"),sQuery(id+"F0.wireOp",EDGE,"E431"),sQuery(id+"F0.wireOp",EDGE,"E432"),sQuery(id+"F0.wireOp",EDGE,"E433"),sQuery(id+"F0.wireOp",EDGE,"E434"),sQuery(id+"F0.wireOp",EDGE,"E435"),sQuery(id+"F0.wireOp",EDGE,"E436"),sQuery(id+"F0.wireOp",EDGE,"E437"),sQuery(id+"F0.wireOp",EDGE,"E438"),sQuery(id+"F0.wireOp",EDGE,"E439"),sQuery(id+"F0.wireOp",EDGE,"E440"),sQuery(id+"F0.wireOp",EDGE,"E441"),sQuery(id+"F0.wireOp",EDGE,"E442"),sQuery(id+"F0.wireOp",EDGE,"E443"),sQuery(id+"F0.wireOp",EDGE,"E444"),sQuery(id+"F0.wireOp",EDGE,"E445"),sQuery(id+"F0.wireOp",EDGE,"E446"),sQuery(id+"F0.wireOp",EDGE,"E447"),sQuery(id+"F0.wireOp",EDGE,"E448"),sQuery(id+"F0.wireOp",EDGE,"E449"),sQuery(id+"F0.wireOp",EDGE,"E450"),sQuery(id+"F0.wireOp",EDGE,"E451"),sQuery(id+"F0.wireOp",EDGE,"E452"),sQuery(id+"F0.wireOp",EDGE,"E453"),sQuery(id+"F0.wireOp",EDGE,"E454"),sQuery(id+"F0.wireOp",EDGE,"E455"),sQuery(id+"F0.wireOp",EDGE,"E456"),sQuery(id+"F0.wireOp",EDGE,"E457"),sQuery(id+"F0.wireOp",EDGE,"E458"),sQuery(id+"F0.wireOp",EDGE,"E459"),sQuery(id+"F0.wireOp",EDGE,"E460"),sQuery(id+"F0.wireOp",EDGE,"E461"),sQuery(id+"F0.wireOp",EDGE,"E462"),sQuery(id+"F0.wireOp",EDGE,"E463"),sQuery(id+"F0.wireOp",EDGE,"E464"),sQuery(id+"F0.wireOp",EDGE,"E465"),sQuery(id+"F0.wireOp",EDGE,"E466"),sQuery(id+"F0.wireOp",EDGE,"E467"),sQuery(id+"F0.wireOp",EDGE,"E468"),sQuery(id+"F0.wireOp",EDGE,"E469"),sQuery(id+"F0.wireOp",EDGE,"E470"),sQuery(id+"F0.wireOp",EDGE,"E471"),sQuery(id+"F0.wireOp",EDGE,"E472"),sQuery(id+"F0.wireOp",EDGE,"E473"),sQuery(id+"F0.wireOp",EDGE,"E474"),sQuery(id+"F0.wireOp",EDGE,"E475"),sQuery(id+"F0.wireOp",EDGE,"E476"),sQuery(id+"F0.wireOp",EDGE,"E477"),sQuery(id+"F0.wireOp",EDGE,"E478"),sQuery(id+"F0.wireOp",EDGE,"E479"),sQuery(id+"F0.wireOp",EDGE,"E480"),sQuery(id+"F0.wireOp",EDGE,"E481"),sQuery(id+"F0.wireOp",EDGE,"E482"),sQuery(id+"F0.wireOp",EDGE,"E483"),sQuery(id+"F0.wireOp",EDGE,"E484"),sQuery(id+"F0.wireOp",EDGE,"E485"),sQuery(id+"F0.wireOp",EDGE,"E486"),sQuery(id+"F0.wireOp",EDGE,"E487"),sQuery(id+"F0.wireOp",EDGE,"E488"),sQuery(id+"F0.wireOp",EDGE,"E489"),sQuery(id+"F0.wireOp",EDGE,"E490"),sQuery(id+"F0.wireOp",EDGE,"E491"),sQuery(id+"F0.wireOp",EDGE,"E492"),sQuery(id+"F0.wireOp",EDGE,"E493"),sQuery(id+"F0.wireOp",EDGE,"E494"),sQuery(id+"F0.wireOp",EDGE,"E495"),sQuery(id+"F0.wireOp",EDGE,"E496"),sQuery(id+"F0.wireOp",EDGE,"E497"),sQuery(id+"F0.wireOp",EDGE,"E498"),sQuery(id+"F0.wireOp",EDGE,"E499"),sQuery(id+"F0.wireOp",EDGE,"E500"),sQuery(id+"F0.wireOp",EDGE,"E501"),sQuery(id+"F0.wireOp",EDGE,"E502"),sQuery(id+"F0.wireOp",EDGE,"E503"),sQuery(id+"F0.wireOp",EDGE,"E504"),sQuery(id+"F0.wireOp",EDGE,"E505"),sQuery(id+"F0.wireOp",EDGE,"E506"),sQuery(id+"F0.wireOp",EDGE,"E507"),sQuery(id+"F0.wireOp",EDGE,"E508"),sQuery(id+"F0.wireOp",EDGE,"E509"),sQuery(id+"F0.wireOp",EDGE,"E510"),sQuery(id+"F0.wireOp",EDGE,"E511"),sQuery(id+"F0.wireOp",EDGE,"E512"),sQuery(id+"F0.wireOp",EDGE,"E513"),sQuery(id+"F0.wireOp",EDGE,"E514"),sQuery(id+"F0.wireOp",EDGE,"E515"),sQuery(id+"F0.wireOp",EDGE,"E516"),sQuery(id+"F0.wireOp",EDGE,"E517"),sQuery(id+"F0.wireOp",EDGE,"E518"),sQuery(id+"F0.wireOp",EDGE,"E519"),sQuery(id+"F0.wireOp",EDGE,"E520"),sQuery(id+"F0.wireOp",EDGE,"E521"),sQuery(id+"F0.wireOp",EDGE,"E522"),sQuery(id+"F0.wireOp",EDGE,"E523"),sQuery(id+"F0.wireOp",EDGE,"E524"),sQuery(id+"F0.wireOp",EDGE,"E525"),sQuery(id+"F0.wireOp",EDGE,"E526"),sQuery(id+"F0.wireOp",EDGE,"E527"),sQuery(id+"F0.wireOp",EDGE,"E528"),sQuery(id+"F0.wireOp",EDGE,"E529"),sQuery(id+"F0.wireOp",EDGE,"E530"),sQuery(id+"F0.wireOp",EDGE,"E531"),sQuery(id+"F0.wireOp",EDGE,"E532"),sQuery(id+"F0.wireOp",EDGE,"E533"),sQuery(id+"F0.wireOp",EDGE,"E534"),sQuery(id+"F0.wireOp",EDGE,"E535"),sQuery(id+"F0.wireOp",EDGE,"E536"),sQuery(id+"F0.wireOp",EDGE,"E537"),sQuery(id+"F0.wireOp",EDGE,"E538"),sQuery(id+"F0.wireOp",EDGE,"E539"),sQuery(id+"F0.wireOp",EDGE,"E540"),sQuery(id+"F0.wireOp",EDGE,"E541"),sQuery(id+"F0.wireOp",EDGE,"E542"),sQuery(id+"F0.wireOp",EDGE,"E543"),sQuery(id+"F0.wireOp",EDGE,"E544"),sQuery(id+"F0.wireOp",EDGE,"E545"),sQuery(id+"F0.wireOp",EDGE,"E546"),sQuery(id+"F0.wireOp",EDGE,"E547"),sQuery(id+"F0.wireOp",EDGE,"E548"),sQuery(id+"F0.wireOp",EDGE,"E549"),sQuery(id+"F0.wireOp",EDGE,"E550"),sQuery(id+"F0.wireOp",EDGE,"E551"),sQuery(id+"F0.wireOp",EDGE,"E552"),sQuery(id+"F0.wireOp",EDGE,"E553"),sQuery(id+"F0.wireOp",EDGE,"E554"),sQuery(id+"F0.wireOp",EDGE,"E555"),sQuery(id+"F0.wireOp",EDGE,"E556"),sQuery(id+"F0.wireOp",EDGE,"E557"),sQuery(id+"F0.wireOp",EDGE,"E558"),sQuery(id+"F0.wireOp",EDGE,"E559"),sQuery(id+"F0.wireOp",EDGE,"E560"),sQuery(id+"F0.wireOp",EDGE,"E561"),sQuery(id+"F0.wireOp",EDGE,"E562"),sQuery(id+"F0.wireOp",EDGE,"E563"),sQuery(id+"F0.wireOp",EDGE,"E564"),sQuery(id+"F0.wireOp",EDGE,"E565"),sQuery(id+"F0.wireOp",EDGE,"E566"),sQuery(id+"F0.wireOp",EDGE,"E567"),sQuery(id+"F0.wireOp",EDGE,"E568"),sQuery(id+"F0.wireOp",EDGE,"E569"),sQuery(id+"F0.wireOp",EDGE,"E570"),sQuery(id+"F0.wireOp",EDGE,"E571"),sQuery(id+"F0.wireOp",EDGE,"E572"),sQuery(id+"F0.wireOp",EDGE,"E573"),sQuery(id+"F0.wireOp",EDGE,"E574"),sQuery(id+"F0.wireOp",EDGE,"E575"),sQuery(id+"F0.wireOp",EDGE,"E576"),sQuery(id+"F0.wireOp",EDGE,"E577"),sQuery(id+"F0.wireOp",EDGE,"E578"),sQuery(id+"F0.wireOp",EDGE,"E579"),sQuery(id+"F0.wireOp",EDGE,"E580"),sQuery(id+"F0.wireOp",EDGE,"E581"),sQuery(id+"F0.wireOp",EDGE,"E582"),sQuery(id+"F0.wireOp",EDGE,"E583"),sQuery(id+"F0.wireOp",EDGE,"E584"),sQuery(id+"F0.wireOp",EDGE,"E585"),sQuery(id+"F0.wireOp",EDGE,"E586"),sQuery(id+"F0.wireOp",EDGE,"E587")])],"isStart":false});
            var sketch = newSketch(context, id + "F2", { "sketchPlane" : qUnion([Q0])});
            skCircle(sketch, "E588", {"center": v(0, 0) * mm, "radius": 4.35 * mm});
            skSolve(sketch);
        }
        {
            var Q0;
            Q0=makeQuery(id+"F2.imprint","IMPRINT",FACE,{"disambiguationData":[TD([[makeQuery(id+"F2.imprint","IMPRINT",EDGE,{"derivedFrom":sQuery(id+"F2.wireOp",EDGE,"E588")}),1.0]])]});
            extrude(context, id + "F3", {"entities" : qUnion([Q0]), "operationType" : NewBodyOperationType.REMOVE, "oppositeDirection" : true, "depth" : 25 * mm});
        }
    });
